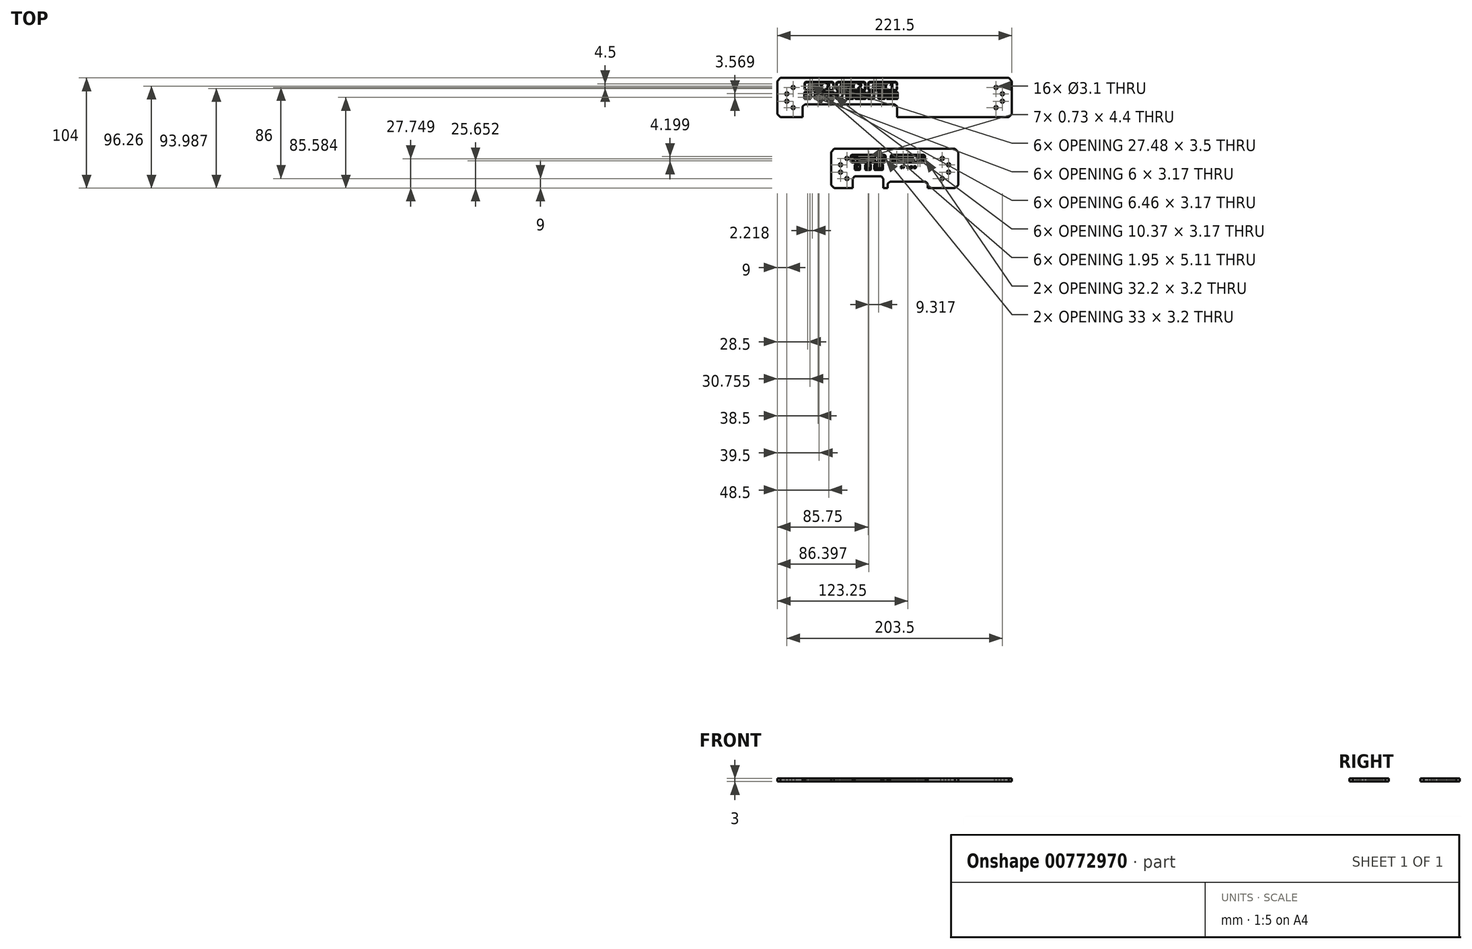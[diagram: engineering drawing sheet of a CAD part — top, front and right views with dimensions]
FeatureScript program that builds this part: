
annotation { "Feature Type Name" : "Feature", "Feature Type Description" : "" }
export const myFeature = defineFeature(function(context is Context, id is Id, definition is map)
    precondition{}
    {
        {
            var Q0;
            Q0=qCreatedBy(makeId("Top.planeOp"),FACE);
            var sketch = newSketch(context, id + "F0", { "sketchPlane" : qUnion([Q0])});
            skLineSegment(sketch, "E0.bottom", {"start": v(110.75, 18.5) * mm, "end": v(-110.75, 18.5) * mm});
            skLineSegment(sketch, "E0.top", {"start": v(110.75, -18.5) * mm, "end": v(-110.75, -18.5) * mm});
            skLineSegment(sketch, "E0.left", {"start": v(110.75, 18.5) * mm, "end": v(110.75, -18.5) * mm});
            skLineSegment(sketch, "E0.right", {"start": v(-110.75, 18.5) * mm, "end": v(-110.75, -18.5) * mm});
            skPoint(sketch, "E0.middle", {"position": v(0, 0) * mm});
            skLineSegment(sketch, "E1", {"start": v(0, 18.5) * mm, "end": v(0, -18.5) * mm, "construction": true});
            skCircle(sketch, "E2", {"center": v(95.75, 9.5) * mm, "radius": 1.55 * mm});
            skCircle(sketch, "E3", {"center": v(101.75, 3.5) * mm, "radius": 1.55 * mm});
            skCircle(sketch, "E4.MirrorC", {"center": v(-95.75, 9.5) * mm, "radius": 1.55 * mm});
            skCircle(sketch, "E5.MirrorC", {"center": v(-101.75, 3.5) * mm, "radius": 1.55 * mm});
            skLineSegment(sketch, "E6.bottom", {"start": v(-85.75, -18.5) * mm, "end": v(1.25, -18.5) * mm});
            skLineSegment(sketch, "E6.top", {"start": v(-85.75, -6.5) * mm, "end": v(1.25, -6.5) * mm});
            skLineSegment(sketch, "E6.left", {"start": v(-85.75, -18.5) * mm, "end": v(-85.75, -6.5) * mm});
            skLineSegment(sketch, "E6.right", {"start": v(1.25, -18.5) * mm, "end": v(1.25, -6.5) * mm});
            skLineSegment(sketch, "E7", {"start": v(-82.25, -6.5) * mm, "end": v(-82.25, -18.5) * mm, "construction": true});
            skLineSegment(sketch, "E8.1.0.0", {"start": v(-72.25, -6.5) * mm, "end": v(-72.25, -18.5) * mm, "construction": true});
            skLineSegment(sketch, "E8.2.0.0", {"start": v(-62.25, -6.5) * mm, "end": v(-62.25, -18.5) * mm, "construction": true});
            skLineSegment(sketch, "E8.3.0.0", {"start": v(-52.25, -6.5) * mm, "end": v(-52.25, -18.5) * mm, "construction": true});
            skLineSegment(sketch, "E8.4.0.0", {"start": v(-42.25, -6.5) * mm, "end": v(-42.25, -18.5) * mm, "construction": true});
            skLineSegment(sketch, "E8.5.0.0", {"start": v(-32.25, -6.5) * mm, "end": v(-32.25, -18.5) * mm, "construction": true});
            skLineSegment(sketch, "E8.6.0.0", {"start": v(-22.25, -6.5) * mm, "end": v(-22.25, -18.5) * mm, "construction": true});
            skLineSegment(sketch, "E8.7.0.0", {"start": v(-12.25, -6.5) * mm, "end": v(-12.25, -18.5) * mm, "construction": true});
            skLineSegment(sketch, "E8.direction1", {"start": v(-82.25, -18.5) * mm, "end": v(-72.25, -18.5) * mm, "construction": true});
            skText(sketch, "E9", { "text": "L", "fontName": "AllertaStencil-Regular.ttf"});
            skText(sketch, "E10", { "text": "N", "fontName": "AllertaStencil-Regular.ttf"});
            skText(sketch, "E11", { "text": "PG", "fontName": "AllertaStencil-Regular.ttf"});
            skText(sketch, "E12", { "text": "L", "fontName": "AllertaStencil-Regular.ttf"});
            skText(sketch, "E13", { "text": "N", "fontName": "AllertaStencil-Regular.ttf"});
            skText(sketch, "E14", { "text": "PG", "fontName": "AllertaStencil-Regular.ttf"});
            skText(sketch, "E15", { "text": "L", "fontName": "AllertaStencil-Regular.ttf"});
            skText(sketch, "E16", { "text": "N", "fontName": "AllertaStencil-Regular.ttf"});
            skText(sketch, "E17", { "text": "PG", "fontName": "AllertaStencil-Regular.ttf"});
            skLineSegment(sketch, "E18.0.8.0", {"start": v(-2.25, -6.5) * mm, "end": v(-2.25, -18.5) * mm, "construction": true});
            skText(sketch, "E19", { "text": "OUT 1", "fontName": "AllertaStencil-Regular.ttf"});
            skText(sketch, "E20", { "text": "OUT 2", "fontName": "AllertaStencil-Regular.ttf"});
            skText(sketch, "E21", { "text": "OUT 3", "fontName": "AllertaStencil-Regular.ttf"});
            skLineSegment(sketch, "E22", {"start": v(-110.75, 0) * mm, "end": v(110.75, 0) * mm, "construction": true});
            skCircle(sketch, "E23.MirrorC", {"center": v(95.75, -9.5) * mm, "radius": 1.55 * mm});
            skCircle(sketch, "E24.MirrorC", {"center": v(101.75, -3.5) * mm, "radius": 1.55 * mm});
            skCircle(sketch, "E25.MirrorC", {"center": v(-95.75, -9.5) * mm, "radius": 1.55 * mm});
            skCircle(sketch, "E26.MirrorC", {"center": v(-101.75, -3.5) * mm, "radius": 1.55 * mm});
            skLineSegment(sketch, "E27", {"start": v(1.25, -6.5) * mm, "end": v(2.25, -6.5) * mm});
            skLineSegment(sketch, "E28", {"start": v(2.25, -6.5) * mm, "end": v(2.25, -18.5) * mm});
            skLineSegment(sketch, "E29", {"start": v(-85.75, -6.5) * mm, "end": v(-86.75, -6.5) * mm});
            skLineSegment(sketch, "E30", {"start": v(-86.75, -6.5) * mm, "end": v(-86.75, -18.5) * mm});
            skLineSegment(sketch, "E31.bottom", {"start": v(60, -48.5) * mm, "end": v(-60, -48.5) * mm});
            skLineSegment(sketch, "E31.top", {"start": v(60, -85.5) * mm, "end": v(-60, -85.5) * mm});
            skLineSegment(sketch, "E31.left", {"start": v(60, -48.5) * mm, "end": v(60, -85.5) * mm});
            skLineSegment(sketch, "E31.right", {"start": v(-60, -48.5) * mm, "end": v(-60, -85.5) * mm});
            skPoint(sketch, "E31.middle", {"position": v(0, -67) * mm});
            skLineSegment(sketch, "E32", {"start": v(-60, -67) * mm, "end": v(60, -67) * mm, "construction": true});
            skLineSegment(sketch, "E33", {"start": v(0, -48.5) * mm, "end": v(0, -85.5) * mm, "construction": true});
            skCircle(sketch, "E34", {"center": v(45, -57.5) * mm, "radius": 1.55 * mm});
            skCircle(sketch, "E35", {"center": v(51, -63.5) * mm, "radius": 1.55 * mm});
            skCircle(sketch, "E36.MirrorC", {"center": v(45, -76.5) * mm, "radius": 1.55 * mm});
            skCircle(sketch, "E37.MirrorC", {"center": v(51, -70.5) * mm, "radius": 1.55 * mm});
            skCircle(sketch, "E38.MirrorC", {"center": v(-45, -57.5) * mm, "radius": 1.55 * mm});
            skCircle(sketch, "E39.MirrorC", {"center": v(-51, -63.5) * mm, "radius": 1.55 * mm});
            skCircle(sketch, "E40.MirrorC", {"center": v(-51, -70.5) * mm, "radius": 1.55 * mm});
            skCircle(sketch, "E41.MirrorC", {"center": v(-45, -76.5) * mm, "radius": 1.55 * mm});
            skLineSegment(sketch, "E42", {"start": v(-39.5, -85.5) * mm, "end": v(-39.5, -74.5) * mm});
            skLineSegment(sketch, "E43", {"start": v(-39.5, -74.5) * mm, "end": v(-10.5, -74.5) * mm});
            skLineSegment(sketch, "E44", {"start": v(-10.5, -74.5) * mm, "end": v(-10.5, -85.5) * mm});
            skLineSegment(sketch, "E45", {"start": v(-6.4, -85.5) * mm, "end": v(-6.4, -79.5) * mm});
            skLineSegment(sketch, "E46", {"start": v(-6.4, -79.5) * mm, "end": v(31.4, -79.5) * mm});
            skLineSegment(sketch, "E47", {"start": v(31.4, -79.5) * mm, "end": v(31.4, -85.5) * mm});
            skLineSegment(sketch, "E48", {"start": v(-38.5, -74.5) * mm, "end": v(-38.5, -85.5) * mm});
            skLineSegment(sketch, "E49", {"start": v(-11.5, -74.5) * mm, "end": v(-11.5, -85.5) * mm});
            skLineSegment(sketch, "E50", {"start": v(-35, -74.5) * mm, "end": v(-35, -85.5) * mm});
            skLineSegment(sketch, "E51", {"start": v(-25, -74.5) * mm, "end": v(-25, -85.5) * mm});
            skLineSegment(sketch, "E52", {"start": v(-15, -74.5) * mm, "end": v(-15, -85.5) * mm});
            skText(sketch, "E53", { "text": "L", "fontName": "AllertaStencil-Regular.ttf"});
            skText(sketch, "E54", { "text": "N", "fontName": "AllertaStencil-Regular.ttf"});
            skText(sketch, "E55", { "text": "POWER IN", "fontName": "AllertaStencil-Regular.ttf"});
            skLineSegment(sketch, "E56.bottom", {"start": v(-84.49, 14.24) * mm, "end": v(-58.01, 14.24) * mm});
            skLineSegment(sketch, "E56.top", {"start": v(-84.49, 7.24) * mm, "end": v(-58.01, 7.24) * mm});
            skLineSegment(sketch, "E56.left", {"start": v(-84.49, 14.24) * mm, "end": v(-84.49, 7.24) * mm});
            skLineSegment(sketch, "E56.right", {"start": v(-58.01, 14.24) * mm, "end": v(-58.01, 7.24) * mm});
            skLineSegment(sketch, "E57.bottom", {"start": v(-57.51, 14.74) * mm, "end": v(-84.99, 14.74) * mm});
            skLineSegment(sketch, "E57.top", {"start": v(-57.51, 6.74) * mm, "end": v(-84.99, 6.74) * mm});
            skLineSegment(sketch, "E57.left", {"start": v(-57.51, 14.74) * mm, "end": v(-57.51, 6.74) * mm});
            skLineSegment(sketch, "E57.right", {"start": v(-84.99, 14.74) * mm, "end": v(-84.99, 6.74) * mm});
            skPoint(sketch, "E57.middle", {"position": v(-71.25, 10.74) * mm});
            skLineSegment(sketch, "E58", {"start": v(-84.99, 10.74) * mm, "end": v(-57.51, 10.74) * mm, "construction": true});
            skLineSegment(sketch, "E59", {"start": v(-84.49, 11.24) * mm, "end": v(-84.99, 11.24) * mm});
            skLineSegment(sketch, "E60.MirrorCS", {"start": v(-84.49, 10.24) * mm, "end": v(-84.99, 10.24) * mm});
            skLineSegment(sketch, "E61.MirrorCS", {"start": v(-58.01, 11.24) * mm, "end": v(-57.51, 11.24) * mm});
            skLineSegment(sketch, "E62.MirrorCS", {"start": v(-58.01, 10.24) * mm, "end": v(-57.51, 10.24) * mm});
            skLineSegment(sketch, "E63.1.0.0", {"start": v(-27.51, 14.74) * mm, "end": v(-54.99, 14.74) * mm});
            skLineSegment(sketch, "E63.1.0.1", {"start": v(-54.49, 14.24) * mm, "end": v(-28.01, 14.24) * mm});
            skLineSegment(sketch, "E63.1.0.2", {"start": v(-54.49, 7.24) * mm, "end": v(-28.01, 7.24) * mm});
            skLineSegment(sketch, "E63.1.0.3", {"start": v(-27.51, 6.74) * mm, "end": v(-54.99, 6.74) * mm});
            skLineSegment(sketch, "E63.1.0.4", {"start": v(-28.01, 14.24) * mm, "end": v(-28.01, 7.24) * mm});
            skLineSegment(sketch, "E63.1.0.5", {"start": v(-27.51, 14.74) * mm, "end": v(-27.51, 6.74) * mm});
            skLineSegment(sketch, "E63.1.0.6", {"start": v(-28.01, 10.24) * mm, "end": v(-27.51, 10.24) * mm});
            skLineSegment(sketch, "E63.1.0.7", {"start": v(-28.01, 11.24) * mm, "end": v(-27.51, 11.24) * mm});
            skLineSegment(sketch, "E63.1.0.8", {"start": v(-54.49, 10.24) * mm, "end": v(-54.99, 10.24) * mm});
            skLineSegment(sketch, "E63.1.0.9", {"start": v(-54.99, 14.74) * mm, "end": v(-54.99, 6.74) * mm});
            skLineSegment(sketch, "E63.1.0.10", {"start": v(-54.49, 14.24) * mm, "end": v(-54.49, 7.24) * mm});
            skLineSegment(sketch, "E63.1.0.11", {"start": v(-54.49, 11.24) * mm, "end": v(-54.99, 11.24) * mm});
            skLineSegment(sketch, "E63.2.0.0", {"start": v(2.49, 14.74) * mm, "end": v(-24.99, 14.74) * mm});
            skLineSegment(sketch, "E63.2.0.1", {"start": v(-24.49, 14.24) * mm, "end": v(1.99, 14.24) * mm});
            skLineSegment(sketch, "E63.2.0.2", {"start": v(-24.49, 7.24) * mm, "end": v(1.99, 7.24) * mm});
            skLineSegment(sketch, "E63.2.0.3", {"start": v(2.49, 6.74) * mm, "end": v(-24.99, 6.74) * mm});
            skLineSegment(sketch, "E63.2.0.4", {"start": v(1.99, 14.24) * mm, "end": v(1.99, 7.24) * mm});
            skLineSegment(sketch, "E63.2.0.5", {"start": v(2.49, 14.74) * mm, "end": v(2.49, 6.74) * mm});
            skLineSegment(sketch, "E63.2.0.6", {"start": v(1.99, 10.24) * mm, "end": v(2.49, 10.24) * mm});
            skLineSegment(sketch, "E63.2.0.7", {"start": v(1.99, 11.24) * mm, "end": v(2.49, 11.24) * mm});
            skLineSegment(sketch, "E63.2.0.8", {"start": v(-24.49, 10.24) * mm, "end": v(-24.99, 10.24) * mm});
            skLineSegment(sketch, "E63.2.0.9", {"start": v(-24.99, 14.74) * mm, "end": v(-24.99, 6.74) * mm});
            skLineSegment(sketch, "E63.2.0.10", {"start": v(-24.49, 14.24) * mm, "end": v(-24.49, 7.24) * mm});
            skLineSegment(sketch, "E63.2.0.11", {"start": v(-24.49, 11.24) * mm, "end": v(-24.99, 11.24) * mm});
            skLineSegment(sketch, "E63.direction1", {"start": v(-84.99, 14.74) * mm, "end": v(-54.99, 14.74) * mm, "construction": true});
            skLineSegment(sketch, "E64.bottom", {"start": v(-79.75, 4.74) * mm, "end": v(-84.75, 4.74) * mm});
            skLineSegment(sketch, "E64.top", {"start": v(-79.75, -1) * mm, "end": v(-84.75, -1) * mm});
            skLineSegment(sketch, "E64.left", {"start": v(-79.75, 4.74) * mm, "end": v(-79.75, -1) * mm});
            skLineSegment(sketch, "E64.right", {"start": v(-84.75, 4.74) * mm, "end": v(-84.75, -1) * mm});
            skPoint(sketch, "E64.middle", {"position": v(-82.25, 1.87) * mm});
            skLineSegment(sketch, "E65.bottom", {"start": v(-69.52, 4.74) * mm, "end": v(-74.98, 4.74) * mm});
            skLineSegment(sketch, "E65.top", {"start": v(-69.52, -1) * mm, "end": v(-74.98, -1) * mm});
            skLineSegment(sketch, "E65.left", {"start": v(-69.52, 4.74) * mm, "end": v(-69.52, -1) * mm});
            skLineSegment(sketch, "E65.right", {"start": v(-74.98, 4.74) * mm, "end": v(-74.98, -1) * mm});
            skPoint(sketch, "E65.middle", {"position": v(-72.25, 1.87) * mm});
            skLineSegment(sketch, "E66.bottom", {"start": v(-66.93, 4.74) * mm, "end": v(-57.57, 4.74) * mm});
            skLineSegment(sketch, "E66.top", {"start": v(-66.93, -1) * mm, "end": v(-57.57, -1) * mm});
            skLineSegment(sketch, "E66.left", {"start": v(-66.93, 4.74) * mm, "end": v(-66.93, -1) * mm});
            skLineSegment(sketch, "E66.right", {"start": v(-57.57, 4.74) * mm, "end": v(-57.57, -1) * mm});
            skLineSegment(sketch, "E67.bottom", {"start": v(-79.25, 5.24) * mm, "end": v(-85.25, 5.24) * mm});
            skLineSegment(sketch, "E67.top", {"start": v(-79.25, -1.5) * mm, "end": v(-85.25, -1.5) * mm});
            skLineSegment(sketch, "E67.left", {"start": v(-79.25, 5.24) * mm, "end": v(-79.25, -1.5) * mm});
            skLineSegment(sketch, "E67.right", {"start": v(-85.25, 5.24) * mm, "end": v(-85.25, -1.5) * mm});
            skLineSegment(sketch, "E68.bottom", {"start": v(-69.02, 5.24) * mm, "end": v(-75.48, 5.24) * mm});
            skLineSegment(sketch, "E68.top", {"start": v(-69.02, -1.5) * mm, "end": v(-75.48, -1.5) * mm});
            skLineSegment(sketch, "E68.left", {"start": v(-69.02, 5.24) * mm, "end": v(-69.02, -1.5) * mm});
            skLineSegment(sketch, "E68.right", {"start": v(-75.48, 5.24) * mm, "end": v(-75.48, -1.5) * mm});
            skPoint(sketch, "E69.firstSnap0", {"position": v(-72.25, 5.24) * mm});
            skLineSegment(sketch, "E69.bottom", {"start": v(-67.43, 5.24) * mm, "end": v(-57.07, 5.24) * mm});
            skLineSegment(sketch, "E69.top", {"start": v(-67.43, -1.5) * mm, "end": v(-57.07, -1.5) * mm});
            skLineSegment(sketch, "E69.left", {"start": v(-67.43, 5.24) * mm, "end": v(-67.43, -1.5) * mm});
            skLineSegment(sketch, "E69.right", {"start": v(-57.07, 5.24) * mm, "end": v(-57.07, -1.5) * mm});
            skLineSegment(sketch, "E70", {"start": v(-85.25, 1.87) * mm, "end": v(-79.25, 1.87) * mm, "construction": true});
            skLineSegment(sketch, "E71", {"start": v(-85.25, 2.07) * mm, "end": v(-84.75, 2.07) * mm});
            skLineSegment(sketch, "E72", {"start": v(-75.48, 2.07) * mm, "end": v(-74.98, 2.07) * mm});
            skLineSegment(sketch, "E73", {"start": v(-67.43, 2.07) * mm, "end": v(-66.93, 2.07) * mm});
            skLineSegment(sketch, "E74.MirrorCS", {"start": v(-85.25, 1.67) * mm, "end": v(-84.75, 1.67) * mm});
            skLineSegment(sketch, "E75.MirrorCS", {"start": v(-75.48, 1.67) * mm, "end": v(-74.98, 1.67) * mm});
            skLineSegment(sketch, "E76.MirrorCS", {"start": v(-67.43, 1.67) * mm, "end": v(-66.93, 1.67) * mm});
            skLineSegment(sketch, "E77.MirrorCS", {"start": v(-79.25, 2.07) * mm, "end": v(-79.75, 2.07) * mm});
            skLineSegment(sketch, "E78.MirrorCS", {"start": v(-79.25, 1.67) * mm, "end": v(-79.75, 1.67) * mm});
            skLineSegment(sketch, "E79.MirrorCS", {"start": v(-69.02, 2.07) * mm, "end": v(-69.52, 2.07) * mm});
            skLineSegment(sketch, "E80.MirrorCS", {"start": v(-69.02, 1.67) * mm, "end": v(-69.52, 1.67) * mm});
            skLineSegment(sketch, "E81.MirrorCS", {"start": v(-57.07, 2.07) * mm, "end": v(-57.57, 2.07) * mm});
            skLineSegment(sketch, "E82.MirrorCS", {"start": v(-57.07, 1.67) * mm, "end": v(-57.57, 1.67) * mm});
            skLineSegment(sketch, "E83.1.0.0", {"start": v(-55.25, 5.24) * mm, "end": v(-55.25, -1.5) * mm});
            skLineSegment(sketch, "E83.1.0.1", {"start": v(-37.43, 5.24) * mm, "end": v(-37.43, -1.5) * mm});
            skLineSegment(sketch, "E83.1.0.2", {"start": v(-39.02, 5.24) * mm, "end": v(-45.48, 5.24) * mm});
            skLineSegment(sketch, "E83.1.0.3", {"start": v(-37.43, 5.24) * mm, "end": v(-27.07, 5.24) * mm});
            skLineSegment(sketch, "E83.1.0.4", {"start": v(-36.93, 4.74) * mm, "end": v(-27.57, 4.74) * mm});
            skLineSegment(sketch, "E83.1.0.5", {"start": v(-39.02, 5.24) * mm, "end": v(-39.02, -1.5) * mm});
            skLineSegment(sketch, "E83.1.0.6", {"start": v(-39.52, -1) * mm, "end": v(-44.98, -1) * mm});
            skLineSegment(sketch, "E83.1.0.7", {"start": v(-36.93, -1) * mm, "end": v(-27.57, -1) * mm});
            skLineSegment(sketch, "E83.1.0.8", {"start": v(-39.02, -1.5) * mm, "end": v(-45.48, -1.5) * mm});
            skLineSegment(sketch, "E83.1.0.9", {"start": v(-49.25, 5.24) * mm, "end": v(-49.25, -1.5) * mm});
            skPoint(sketch, "E83.1.0.10", {"position": v(-42.25, 1.87) * mm});
            skLineSegment(sketch, "E83.1.0.11", {"start": v(-49.25, -1.5) * mm, "end": v(-55.25, -1.5) * mm});
            skLineSegment(sketch, "E83.1.0.12", {"start": v(-54.75, 4.74) * mm, "end": v(-54.75, -1) * mm});
            skLineSegment(sketch, "E83.1.0.13", {"start": v(-36.93, 4.74) * mm, "end": v(-36.93, -1) * mm});
            skLineSegment(sketch, "E83.1.0.14", {"start": v(-49.75, -1) * mm, "end": v(-54.75, -1) * mm});
            skPoint(sketch, "E83.1.0.15", {"position": v(-42.25, 5.24) * mm});
            skLineSegment(sketch, "E83.1.0.16", {"start": v(-44.98, 4.74) * mm, "end": v(-44.98, -1) * mm});
            skPoint(sketch, "E83.1.0.17", {"position": v(-52.25, 1.87) * mm});
            skLineSegment(sketch, "E83.1.0.18", {"start": v(-39.52, 4.74) * mm, "end": v(-39.52, -1) * mm});
            skLineSegment(sketch, "E83.1.0.19", {"start": v(-39.52, 4.74) * mm, "end": v(-44.98, 4.74) * mm});
            skLineSegment(sketch, "E83.1.0.20", {"start": v(-45.48, 5.24) * mm, "end": v(-45.48, -1.5) * mm});
            skLineSegment(sketch, "E83.1.0.21", {"start": v(-27.07, 5.24) * mm, "end": v(-27.07, -1.5) * mm});
            skLineSegment(sketch, "E83.1.0.22", {"start": v(-37.43, -1.5) * mm, "end": v(-27.07, -1.5) * mm});
            skLineSegment(sketch, "E83.1.0.23", {"start": v(-49.75, 4.74) * mm, "end": v(-54.75, 4.74) * mm});
            skLineSegment(sketch, "E83.1.0.24", {"start": v(-49.75, 4.74) * mm, "end": v(-49.75, -1) * mm});
            skLineSegment(sketch, "E83.1.0.25", {"start": v(-49.25, 5.24) * mm, "end": v(-55.25, 5.24) * mm});
            skLineSegment(sketch, "E83.1.0.26", {"start": v(-27.57, 4.74) * mm, "end": v(-27.57, -1) * mm});
            skPoint(sketch, "E83.1.0.27", {"position": v(-52.25, 1.87) * mm});
            skLineSegment(sketch, "E83.1.0.28", {"start": v(-45.48, 2.07) * mm, "end": v(-44.98, 2.07) * mm});
            skLineSegment(sketch, "E83.1.0.29", {"start": v(-45.48, 1.67) * mm, "end": v(-44.98, 1.67) * mm});
            skLineSegment(sketch, "E83.1.0.30", {"start": v(-39.02, 1.67) * mm, "end": v(-39.52, 1.67) * mm});
            skLineSegment(sketch, "E83.1.0.31", {"start": v(-27.07, 1.67) * mm, "end": v(-27.57, 1.67) * mm});
            skLineSegment(sketch, "E83.1.0.32", {"start": v(-55.25, 1.67) * mm, "end": v(-54.75, 1.67) * mm});
            skLineSegment(sketch, "E83.1.0.33", {"start": v(-55.25, 2.07) * mm, "end": v(-54.75, 2.07) * mm});
            skLineSegment(sketch, "E83.1.0.34", {"start": v(-37.43, 1.67) * mm, "end": v(-36.93, 1.67) * mm});
            skLineSegment(sketch, "E83.1.0.35", {"start": v(-27.07, 2.07) * mm, "end": v(-27.57, 2.07) * mm});
            skLineSegment(sketch, "E83.1.0.36", {"start": v(-37.43, 2.07) * mm, "end": v(-36.93, 2.07) * mm});
            skLineSegment(sketch, "E83.1.0.37", {"start": v(-39.02, 2.07) * mm, "end": v(-39.52, 2.07) * mm});
            skLineSegment(sketch, "E83.1.0.38", {"start": v(-49.25, 1.67) * mm, "end": v(-49.75, 1.67) * mm});
            skLineSegment(sketch, "E83.1.0.39", {"start": v(-49.25, 2.07) * mm, "end": v(-49.75, 2.07) * mm});
            skLineSegment(sketch, "E83.2.0.0", {"start": v(-25.25, 5.24) * mm, "end": v(-25.25, -1.5) * mm});
            skLineSegment(sketch, "E83.2.0.1", {"start": v(-7.43, 5.24) * mm, "end": v(-7.43, -1.5) * mm});
            skLineSegment(sketch, "E83.2.0.2", {"start": v(-9.02, 5.24) * mm, "end": v(-15.48, 5.24) * mm});
            skLineSegment(sketch, "E83.2.0.3", {"start": v(-7.43, 5.24) * mm, "end": v(2.93, 5.24) * mm});
            skLineSegment(sketch, "E83.2.0.4", {"start": v(-6.93, 4.74) * mm, "end": v(2.43, 4.74) * mm});
            skLineSegment(sketch, "E83.2.0.5", {"start": v(-9.02, 5.24) * mm, "end": v(-9.02, -1.5) * mm});
            skLineSegment(sketch, "E83.2.0.6", {"start": v(-9.52, -1) * mm, "end": v(-14.98, -1) * mm});
            skLineSegment(sketch, "E83.2.0.7", {"start": v(-6.93, -1) * mm, "end": v(2.43, -1) * mm});
            skLineSegment(sketch, "E83.2.0.8", {"start": v(-9.02, -1.5) * mm, "end": v(-15.48, -1.5) * mm});
            skLineSegment(sketch, "E83.2.0.9", {"start": v(-19.25, 5.24) * mm, "end": v(-19.25, -1.5) * mm});
            skPoint(sketch, "E83.2.0.10", {"position": v(-12.25, 1.87) * mm});
            skLineSegment(sketch, "E83.2.0.11", {"start": v(-19.25, -1.5) * mm, "end": v(-25.25, -1.5) * mm});
            skLineSegment(sketch, "E83.2.0.12", {"start": v(-24.75, 4.74) * mm, "end": v(-24.75, -1) * mm});
            skLineSegment(sketch, "E83.2.0.13", {"start": v(-6.93, 4.74) * mm, "end": v(-6.93, -1) * mm});
            skLineSegment(sketch, "E83.2.0.14", {"start": v(-19.75, -1) * mm, "end": v(-24.75, -1) * mm});
            skPoint(sketch, "E83.2.0.15", {"position": v(-12.25, 5.24) * mm});
            skLineSegment(sketch, "E83.2.0.16", {"start": v(-14.98, 4.74) * mm, "end": v(-14.98, -1) * mm});
            skPoint(sketch, "E83.2.0.17", {"position": v(-22.25, 1.87) * mm});
            skLineSegment(sketch, "E83.2.0.18", {"start": v(-9.52, 4.74) * mm, "end": v(-9.52, -1) * mm});
            skLineSegment(sketch, "E83.2.0.19", {"start": v(-9.52, 4.74) * mm, "end": v(-14.98, 4.74) * mm});
            skLineSegment(sketch, "E83.2.0.20", {"start": v(-15.48, 5.24) * mm, "end": v(-15.48, -1.5) * mm});
            skLineSegment(sketch, "E83.2.0.21", {"start": v(2.93, 5.24) * mm, "end": v(2.93, -1.5) * mm});
            skLineSegment(sketch, "E83.2.0.22", {"start": v(-7.43, -1.5) * mm, "end": v(2.93, -1.5) * mm});
            skLineSegment(sketch, "E83.2.0.23", {"start": v(-19.75, 4.74) * mm, "end": v(-24.75, 4.74) * mm});
            skLineSegment(sketch, "E83.2.0.24", {"start": v(-19.75, 4.74) * mm, "end": v(-19.75, -1) * mm});
            skLineSegment(sketch, "E83.2.0.25", {"start": v(-19.25, 5.24) * mm, "end": v(-25.25, 5.24) * mm});
            skLineSegment(sketch, "E83.2.0.26", {"start": v(2.43, 4.74) * mm, "end": v(2.43, -1) * mm});
            skPoint(sketch, "E83.2.0.27", {"position": v(-22.25, 1.87) * mm});
            skLineSegment(sketch, "E83.2.0.28", {"start": v(-15.48, 2.07) * mm, "end": v(-14.98, 2.07) * mm});
            skLineSegment(sketch, "E83.2.0.29", {"start": v(-15.48, 1.67) * mm, "end": v(-14.98, 1.67) * mm});
            skLineSegment(sketch, "E83.2.0.30", {"start": v(-9.02, 1.67) * mm, "end": v(-9.52, 1.67) * mm});
            skLineSegment(sketch, "E83.2.0.31", {"start": v(2.93, 1.67) * mm, "end": v(2.43, 1.67) * mm});
            skLineSegment(sketch, "E83.2.0.32", {"start": v(-25.25, 1.67) * mm, "end": v(-24.75, 1.67) * mm});
            skLineSegment(sketch, "E83.2.0.33", {"start": v(-25.25, 2.07) * mm, "end": v(-24.75, 2.07) * mm});
            skLineSegment(sketch, "E83.2.0.34", {"start": v(-7.43, 1.67) * mm, "end": v(-6.93, 1.67) * mm});
            skLineSegment(sketch, "E83.2.0.35", {"start": v(2.93, 2.07) * mm, "end": v(2.43, 2.07) * mm});
            skLineSegment(sketch, "E83.2.0.36", {"start": v(-7.43, 2.07) * mm, "end": v(-6.93, 2.07) * mm});
            skLineSegment(sketch, "E83.2.0.37", {"start": v(-9.02, 2.07) * mm, "end": v(-9.52, 2.07) * mm});
            skLineSegment(sketch, "E83.2.0.38", {"start": v(-19.25, 1.67) * mm, "end": v(-19.75, 1.67) * mm});
            skLineSegment(sketch, "E83.2.0.39", {"start": v(-19.25, 2.07) * mm, "end": v(-19.75, 2.07) * mm});
            skLineSegment(sketch, "E83.direction1", {"start": v(-85.25, -1.5) * mm, "end": v(-55.25, -1.5) * mm, "construction": true});
            skLineSegment(sketch, "E84.bottom", {"start": v(-9, -54.55) * mm, "end": v(-41, -54.55) * mm});
            skLineSegment(sketch, "E84.top", {"start": v(-9, -60.95) * mm, "end": v(-41, -60.95) * mm});
            skLineSegment(sketch, "E84.left", {"start": v(-9, -54.55) * mm, "end": v(-9, -60.95) * mm});
            skLineSegment(sketch, "E84.right", {"start": v(-41, -54.55) * mm, "end": v(-41, -60.95) * mm});
            skPoint(sketch, "E84.middle", {"position": v(-25, -57.75) * mm});
            skLineSegment(sketch, "E85.bottom", {"start": v(-33, -63.45) * mm, "end": v(-37, -63.45) * mm});
            skLineSegment(sketch, "E85.top", {"start": v(-33, -68) * mm, "end": v(-37, -68) * mm});
            skLineSegment(sketch, "E85.left", {"start": v(-33, -63.45) * mm, "end": v(-33, -68) * mm});
            skLineSegment(sketch, "E85.right", {"start": v(-37, -63.45) * mm, "end": v(-37, -68) * mm});
            skPoint(sketch, "E85.middle", {"position": v(-35, -65.72) * mm});
            skLineSegment(sketch, "E86.bottom", {"start": v(-8.5, -54.05) * mm, "end": v(-41.5, -54.05) * mm});
            skLineSegment(sketch, "E86.top", {"start": v(-8.5, -61.45) * mm, "end": v(-41.5, -61.45) * mm});
            skLineSegment(sketch, "E86.left", {"start": v(-8.5, -54.05) * mm, "end": v(-8.5, -61.45) * mm});
            skLineSegment(sketch, "E86.right", {"start": v(-41.5, -54.05) * mm, "end": v(-41.5, -61.45) * mm});
            skLineSegment(sketch, "E87.bottom", {"start": v(-27.17, -63.45) * mm, "end": v(-22.83, -63.45) * mm});
            skLineSegment(sketch, "E87.top", {"start": v(-27.17, -68) * mm, "end": v(-22.83, -68) * mm});
            skLineSegment(sketch, "E87.left", {"start": v(-27.17, -63.45) * mm, "end": v(-27.17, -68) * mm});
            skLineSegment(sketch, "E87.right", {"start": v(-22.83, -63.45) * mm, "end": v(-22.83, -68) * mm});
            skText(sketch, "E88", { "text": "PG", "fontName": "AllertaStencil-Regular.ttf"});
            skLineSegment(sketch, "E89.bottom", {"start": v(-18.64, -63.45) * mm, "end": v(-11.36, -63.45) * mm});
            skLineSegment(sketch, "E89.top", {"start": v(-18.64, -68) * mm, "end": v(-11.36, -68) * mm});
            skLineSegment(sketch, "E89.left", {"start": v(-18.64, -63.45) * mm, "end": v(-18.64, -68) * mm});
            skLineSegment(sketch, "E89.right", {"start": v(-11.36, -63.45) * mm, "end": v(-11.36, -68) * mm});
            skLineSegment(sketch, "E90.bottom", {"start": v(-32.5, -62.95) * mm, "end": v(-37.5, -62.95) * mm});
            skLineSegment(sketch, "E90.top", {"start": v(-32.5, -68.5) * mm, "end": v(-37.5, -68.5) * mm});
            skLineSegment(sketch, "E90.left", {"start": v(-32.5, -62.95) * mm, "end": v(-32.5, -68.5) * mm});
            skLineSegment(sketch, "E90.right", {"start": v(-37.5, -62.95) * mm, "end": v(-37.5, -68.5) * mm});
            skLineSegment(sketch, "E91.bottom", {"start": v(-27.67, -62.95) * mm, "end": v(-22.33, -62.95) * mm});
            skLineSegment(sketch, "E91.top", {"start": v(-27.67, -68.5) * mm, "end": v(-22.33, -68.5) * mm});
            skLineSegment(sketch, "E91.left", {"start": v(-27.67, -62.95) * mm, "end": v(-27.67, -68.5) * mm});
            skLineSegment(sketch, "E91.right", {"start": v(-22.33, -62.95) * mm, "end": v(-22.33, -68.5) * mm});
            skLineSegment(sketch, "E92.bottom", {"start": v(-19.14, -62.95) * mm, "end": v(-10.86, -62.95) * mm});
            skLineSegment(sketch, "E92.top", {"start": v(-19.14, -68.5) * mm, "end": v(-10.86, -68.5) * mm});
            skLineSegment(sketch, "E92.left", {"start": v(-19.14, -62.95) * mm, "end": v(-19.14, -68.5) * mm});
            skLineSegment(sketch, "E92.right", {"start": v(-10.86, -62.95) * mm, "end": v(-10.86, -68.5) * mm});
            skLineSegment(sketch, "E93", {"start": v(-37.5, -65.72) * mm, "end": v(-32.5, -65.72) * mm, "construction": true});
            skLineSegment(sketch, "E94", {"start": v(-37.5, -65.52) * mm, "end": v(-37, -65.52) * mm});
            skLineSegment(sketch, "E95", {"start": v(-27.67, -65.52) * mm, "end": v(-27.17, -65.52) * mm});
            skLineSegment(sketch, "E96", {"start": v(-19.14, -65.52) * mm, "end": v(-18.64, -65.52) * mm});
            skLineSegment(sketch, "E97", {"start": v(-41.5, -57.75) * mm, "end": v(-8.5, -57.75) * mm, "construction": true});
            skLineSegment(sketch, "E98.MirrorCS", {"start": v(-37.5, -65.92) * mm, "end": v(-37, -65.92) * mm});
            skLineSegment(sketch, "E99.MirrorCS", {"start": v(-27.67, -65.92) * mm, "end": v(-27.17, -65.92) * mm});
            skLineSegment(sketch, "E100.MirrorCS", {"start": v(-19.14, -65.92) * mm, "end": v(-18.64, -65.92) * mm});
            skLineSegment(sketch, "E101.MirrorCS", {"start": v(-32.5, -65.52) * mm, "end": v(-33, -65.52) * mm});
            skLineSegment(sketch, "E102.MirrorCS", {"start": v(-32.5, -65.92) * mm, "end": v(-33, -65.92) * mm});
            skLineSegment(sketch, "E103.MirrorCS", {"start": v(-22.33, -65.52) * mm, "end": v(-22.83, -65.52) * mm});
            skLineSegment(sketch, "E104.MirrorCS", {"start": v(-22.33, -65.92) * mm, "end": v(-22.83, -65.92) * mm});
            skLineSegment(sketch, "E105.MirrorCS", {"start": v(-10.86, -65.52) * mm, "end": v(-11.36, -65.52) * mm});
            skLineSegment(sketch, "E106.MirrorCS", {"start": v(-10.86, -65.92) * mm, "end": v(-11.36, -65.92) * mm});
            skLineSegment(sketch, "E107", {"start": v(-41.5, -57.25) * mm, "end": v(-41, -57.25) * mm});
            skLineSegment(sketch, "E108.MirrorCS", {"start": v(-41.5, -58.25) * mm, "end": v(-41, -58.25) * mm});
            skLineSegment(sketch, "E109.MirrorCS", {"start": v(-8.5, -57.25) * mm, "end": v(-9, -57.25) * mm});
            skLineSegment(sketch, "E110.MirrorCS", {"start": v(-8.5, -58.25) * mm, "end": v(-9, -58.25) * mm});
            skText(sketch, "E111", { "text": "SIGNAL IN", "fontName": "AllertaStencil-Regular.ttf"});
            skLineSegment(sketch, "E112", {"start": v(12.5, -79.5) * mm, "end": v(12.5, -85.5) * mm, "construction": true});
            skLineSegment(sketch, "E113.bottom", {"start": v(-3.1, -54.55) * mm, "end": v(28.1, -54.55) * mm});
            skLineSegment(sketch, "E113.top", {"start": v(-3.1, -60.95) * mm, "end": v(28.1, -60.95) * mm});
            skLineSegment(sketch, "E113.left", {"start": v(-3.1, -54.55) * mm, "end": v(-3.1, -60.95) * mm});
            skLineSegment(sketch, "E113.right", {"start": v(28.1, -54.55) * mm, "end": v(28.1, -60.95) * mm});
            skLineSegment(sketch, "E114.bottom", {"start": v(-3.6, -54.05) * mm, "end": v(28.6, -54.05) * mm});
            skLineSegment(sketch, "E114.top", {"start": v(-3.6, -61.45) * mm, "end": v(28.6, -61.45) * mm});
            skLineSegment(sketch, "E114.left", {"start": v(-3.6, -54.05) * mm, "end": v(-3.6, -61.45) * mm});
            skLineSegment(sketch, "E114.right", {"start": v(28.6, -54.05) * mm, "end": v(28.6, -61.45) * mm});
            skLineSegment(sketch, "E115", {"start": v(-3.6, -57.75) * mm, "end": v(28.6, -57.75) * mm, "construction": true});
            skLineSegment(sketch, "E116", {"start": v(-3.6, -57.25) * mm, "end": v(-3.1, -57.25) * mm});
            skLineSegment(sketch, "E117.MirrorCS", {"start": v(-3.6, -58.25) * mm, "end": v(-3.1, -58.25) * mm});
            skLineSegment(sketch, "E118.MirrorCS", {"start": v(28.6, -57.25) * mm, "end": v(28.1, -57.25) * mm});
            skLineSegment(sketch, "E119.MirrorCS", {"start": v(28.6, -58.25) * mm, "end": v(28.1, -58.25) * mm});
            skText(sketch, "E120", { "text": "S", "fontName": "AllertaStencil-Regular.ttf"});
            skLineSegment(sketch, "E121", {"start": v(11.72, -65.72) * mm, "end": v(13.28, -65.72) * mm, "construction": true});
            skText(sketch, "E122", { "text": "GND", "fontName": "AllertaStencil-Regular.ttf"});
            skText(sketch, "E123", { "text": "5V", "fontName": "AllertaStencil-Regular.ttf"});
            const initialGuessF0  = {"E9": [-0.08425, -0.0005, 1, 0, 0.00474], "E10": [-0.07448, -0.0005, 1, 0, 0.00474], "E11": [-0.06643, -0.0005, 1, 0, 0.00474], "E12": [-0.05425, -0.0005, 1, 0, 0.00474], "E13": [-0.04448, -0.0005, 1, 0, 0.00474], "E14": [-0.03643, -0.0005, 1, 0, 0.00474], "E15": [-0.02425, -0.0005, 1, 0, 0.00474], "E16": [-0.01448, -0.0005, 1, 0, 0.00474], "E17": [-0.00643, -0.0005, 1, 0, 0.00474], "E19": [-0.0209, 0.00824, 1, 0, 0.005], "E20": [-0.05161, 0.00824, 1, 0, 0.005], "E21": [-0.08149, 0.00824, 1, 0, 0.005], "E53": [-0.0365, -0.0675, 1, 0, 0.00355], "E54": [-0.02667, -0.0675, 1, 0, 0.00355], "E55": [-0.04, -0.05995, 1, 0, 0.0044], "E88": [-0.01814, -0.0675, 1, 0, 0.00355], "E111": [-0.0021, -0.05995, 1, 0, 0.0044], "E120": [0.01172, -0.06672, 1, 0, 0.002], "E122": [0.01454, -0.06672, 1, 0, 0.002], "E123": [0.00566, -0.06672, 1, 0, 0.002]};
            skSetInitialGuess(sketch, initialGuessF0);
            skSolve(sketch);
        }
        {
            var Q0;
            Q0=makeQuery(id+"F0.imprint","IMPRINT",FACE,{"disambiguationData":[TD([[makeQuery(id+"F0.imprint","IMPRINT",EDGE,{"derivedFrom":sQuery(id+"F0.wireOp",EDGE,"E0.bottom")}),1.0]])]});
            var Q1;
            {var subQ0=sQuery(id+"F0.wireOp",EDGE,"E59");Q1=makeQuery(id+"F0.imprint","IMPRINT",FACE,{"disambiguationData":[TD([[makeQuery(id+"F0.imprint","IMPRINT",EDGE,{"derivedFrom":subQ0}),1.0]])]});}
            var Q2;
            {var subQ0=sQuery(id+"F0.wireOp",EDGE,"E61.MirrorCS");Q2=makeQuery(id+"F0.imprint","IMPRINT",FACE,{"disambiguationData":[TD([[makeQuery(id+"F0.imprint","IMPRINT",EDGE,{"derivedFrom":subQ0}),-1.0]])]});}
            var Q3;
            {var subQ0=sQuery(id+"F0.wireOp",EDGE,"E81.MirrorCS");Q3=makeQuery(id+"F0.imprint","IMPRINT",FACE,{"disambiguationData":[TD([[makeQuery(id+"F0.imprint","IMPRINT",EDGE,{"derivedFrom":subQ0}),1.0]])]});}
            var Q4;
            Q4=makeQuery(id+"F0.imprint","IMPRINT",FACE,{"disambiguationData":[TD([[makeQuery(id+"F0.imprint","IMPRINT",EDGE,{"derivedFrom":sQuery(id+"F0.wireOp",EDGE,"E11.sketch_text.stroke-0")}),1.0]])]});
            var Q5;
            {var subQ0=sQuery(id+"F0.wireOp",EDGE,"E73");Q5=makeQuery(id+"F0.imprint","IMPRINT",FACE,{"disambiguationData":[TD([[makeQuery(id+"F0.imprint","IMPRINT",EDGE,{"derivedFrom":subQ0}),-1.0]])]});}
            var Q6;
            {var subQ0=sQuery(id+"F0.wireOp",EDGE,"E79.MirrorCS");Q6=makeQuery(id+"F0.imprint","IMPRINT",FACE,{"disambiguationData":[TD([[makeQuery(id+"F0.imprint","IMPRINT",EDGE,{"derivedFrom":subQ0}),1.0]])]});}
            var Q7;
            {var subQ0=sQuery(id+"F0.wireOp",EDGE,"E72");Q7=makeQuery(id+"F0.imprint","IMPRINT",FACE,{"disambiguationData":[TD([[makeQuery(id+"F0.imprint","IMPRINT",EDGE,{"derivedFrom":subQ0}),-1.0]])]});}
            var Q8;
            {var subQ0=sQuery(id+"F0.wireOp",EDGE,"E77.MirrorCS");Q8=makeQuery(id+"F0.imprint","IMPRINT",FACE,{"disambiguationData":[TD([[makeQuery(id+"F0.imprint","IMPRINT",EDGE,{"derivedFrom":subQ0}),1.0]])]});}
            var Q9;
            {var subQ0=sQuery(id+"F0.wireOp",EDGE,"E71");Q9=makeQuery(id+"F0.imprint","IMPRINT",FACE,{"disambiguationData":[TD([[makeQuery(id+"F0.imprint","IMPRINT",EDGE,{"derivedFrom":subQ0}),-1.0]])]});}
            var Q10;
            Q10=makeQuery(id+"F0.imprint","IMPRINT",FACE,{"disambiguationData":[TD([[makeQuery(id+"F0.imprint","IMPRINT",EDGE,{"derivedFrom":sQuery(id+"F0.wireOp",EDGE,"E9.sketch_text.stroke-0")}),1.0]])]});
            var Q11;
            Q11=makeQuery(id+"F0.imprint","IMPRINT",FACE,{"disambiguationData":[TD([[makeQuery(id+"F0.imprint","IMPRINT",EDGE,{"derivedFrom":sQuery(id+"F0.wireOp",EDGE,"E10.sketch_text.stroke-0")}),1.0]])]});
            var Q12;
            Q12=makeQuery(id+"F0.imprint","IMPRINT",FACE,{"disambiguationData":[TD([[makeQuery(id+"F0.imprint","IMPRINT",EDGE,{"derivedFrom":sQuery(id+"F0.wireOp",EDGE,"E21.sketch_text.stroke-0")}),1.0]])]});
            var Q13;
            Q13=makeQuery(id+"F0.imprint","IMPRINT",FACE,{"disambiguationData":[TD([[makeQuery(id+"F0.imprint","IMPRINT",EDGE,{"derivedFrom":sQuery(id+"F0.wireOp",EDGE,"E20.sketch_text.stroke-0")}),1.0]])]});
            var Q14;
            {var subQ0=sQuery(id+"F0.wireOp",EDGE,"E63.1.0.8");Q14=makeQuery(id+"F0.imprint","IMPRINT",FACE,{"disambiguationData":[TD([[makeQuery(id+"F0.imprint","IMPRINT",EDGE,{"derivedFrom":subQ0}),-1.0]])]});}
            var Q15;
            Q15=makeQuery(id+"F0.imprint","IMPRINT",FACE,{"disambiguationData":[TD([[makeQuery(id+"F0.imprint","IMPRINT",EDGE,{"derivedFrom":sQuery(id+"F0.wireOp",EDGE,"E12.sketch_text.stroke-0")}),1.0]])]});
            var Q16;
            {var subQ0=sQuery(id+"F0.wireOp",EDGE,"E83.1.0.32");Q16=makeQuery(id+"F0.imprint","IMPRINT",FACE,{"disambiguationData":[TD([[makeQuery(id+"F0.imprint","IMPRINT",EDGE,{"derivedFrom":subQ0}),1.0]])]});}
            var Q17;
            {var subQ0=sQuery(id+"F0.wireOp",EDGE,"E83.1.0.38");Q17=makeQuery(id+"F0.imprint","IMPRINT",FACE,{"disambiguationData":[TD([[makeQuery(id+"F0.imprint","IMPRINT",EDGE,{"derivedFrom":subQ0}),-1.0]])]});}
            var Q18;
            Q18=makeQuery(id+"F0.imprint","IMPRINT",FACE,{"disambiguationData":[TD([[makeQuery(id+"F0.imprint","IMPRINT",EDGE,{"derivedFrom":sQuery(id+"F0.wireOp",EDGE,"E19.sketch_text.stroke-0")}),1.0]])]});
            var Q19;
            {var subQ0=sQuery(id+"F0.wireOp",EDGE,"E63.2.0.8");Q19=makeQuery(id+"F0.imprint","IMPRINT",FACE,{"disambiguationData":[TD([[makeQuery(id+"F0.imprint","IMPRINT",EDGE,{"derivedFrom":subQ0}),-1.0]])]});}
            var Q20;
            {var subQ0=sQuery(id+"F0.wireOp",EDGE,"E63.1.0.6");Q20=makeQuery(id+"F0.imprint","IMPRINT",FACE,{"disambiguationData":[TD([[makeQuery(id+"F0.imprint","IMPRINT",EDGE,{"derivedFrom":subQ0}),1.0]])]});}
            var Q21;
            {var subQ0=sQuery(id+"F0.wireOp",EDGE,"E83.1.0.28");Q21=makeQuery(id+"F0.imprint","IMPRINT",FACE,{"disambiguationData":[TD([[makeQuery(id+"F0.imprint","IMPRINT",EDGE,{"derivedFrom":subQ0}),-1.0]])]});}
            var Q22;
            {var subQ0=sQuery(id+"F0.wireOp",EDGE,"E83.1.0.30");Q22=makeQuery(id+"F0.imprint","IMPRINT",FACE,{"disambiguationData":[TD([[makeQuery(id+"F0.imprint","IMPRINT",EDGE,{"derivedFrom":subQ0}),-1.0]])]});}
            var Q23;
            {var subQ0=sQuery(id+"F0.wireOp",EDGE,"E83.1.0.34");Q23=makeQuery(id+"F0.imprint","IMPRINT",FACE,{"disambiguationData":[TD([[makeQuery(id+"F0.imprint","IMPRINT",EDGE,{"derivedFrom":subQ0}),1.0]])]});}
            var Q24;
            {var subQ0=sQuery(id+"F0.wireOp",EDGE,"E83.1.0.31");Q24=makeQuery(id+"F0.imprint","IMPRINT",FACE,{"disambiguationData":[TD([[makeQuery(id+"F0.imprint","IMPRINT",EDGE,{"derivedFrom":subQ0}),-1.0]])]});}
            var Q25;
            {var subQ0=sQuery(id+"F0.wireOp",EDGE,"E83.2.0.32");Q25=makeQuery(id+"F0.imprint","IMPRINT",FACE,{"disambiguationData":[TD([[makeQuery(id+"F0.imprint","IMPRINT",EDGE,{"derivedFrom":subQ0}),1.0]])]});}
            var Q26;
            {var subQ0=sQuery(id+"F0.wireOp",EDGE,"E83.2.0.38");Q26=makeQuery(id+"F0.imprint","IMPRINT",FACE,{"disambiguationData":[TD([[makeQuery(id+"F0.imprint","IMPRINT",EDGE,{"derivedFrom":subQ0}),-1.0]])]});}
            var Q27;
            {var subQ0=sQuery(id+"F0.wireOp",EDGE,"E83.2.0.28");Q27=makeQuery(id+"F0.imprint","IMPRINT",FACE,{"disambiguationData":[TD([[makeQuery(id+"F0.imprint","IMPRINT",EDGE,{"derivedFrom":subQ0}),-1.0]])]});}
            var Q28;
            {var subQ0=sQuery(id+"F0.wireOp",EDGE,"E83.2.0.30");Q28=makeQuery(id+"F0.imprint","IMPRINT",FACE,{"disambiguationData":[TD([[makeQuery(id+"F0.imprint","IMPRINT",EDGE,{"derivedFrom":subQ0}),-1.0]])]});}
            var Q29;
            {var subQ0=sQuery(id+"F0.wireOp",EDGE,"E83.2.0.34");Q29=makeQuery(id+"F0.imprint","IMPRINT",FACE,{"disambiguationData":[TD([[makeQuery(id+"F0.imprint","IMPRINT",EDGE,{"derivedFrom":subQ0}),1.0]])]});}
            var Q30;
            Q30=makeQuery(id+"F0.imprint","IMPRINT",FACE,{"disambiguationData":[TD([[makeQuery(id+"F0.imprint","IMPRINT",EDGE,{"derivedFrom":sQuery(id+"F0.wireOp",EDGE,"E17.sketch_text.stroke-0")}),1.0]])]});
            var Q31;
            Q31=makeQuery(id+"F0.imprint","IMPRINT",FACE,{"disambiguationData":[TD([[makeQuery(id+"F0.imprint","IMPRINT",EDGE,{"derivedFrom":sQuery(id+"F0.wireOp",EDGE,"E16.sketch_text.stroke-0")}),1.0]])]});
            var Q32;
            Q32=makeQuery(id+"F0.imprint","IMPRINT",FACE,{"disambiguationData":[TD([[makeQuery(id+"F0.imprint","IMPRINT",EDGE,{"derivedFrom":sQuery(id+"F0.wireOp",EDGE,"E15.sketch_text.stroke-0")}),1.0]])]});
            var Q33;
            Q33=makeQuery(id+"F0.imprint","IMPRINT",FACE,{"disambiguationData":[TD([[makeQuery(id+"F0.imprint","IMPRINT",EDGE,{"derivedFrom":sQuery(id+"F0.wireOp",EDGE,"E14.sketch_text.stroke-0")}),1.0]])]});
            var Q34;
            Q34=makeQuery(id+"F0.imprint","IMPRINT",FACE,{"disambiguationData":[TD([[makeQuery(id+"F0.imprint","IMPRINT",EDGE,{"derivedFrom":sQuery(id+"F0.wireOp",EDGE,"E13.sketch_text.stroke-0")}),1.0]])]});
            var Q35;
            {var subQ0=sQuery(id+"F0.wireOp",EDGE,"E83.2.0.31");Q35=makeQuery(id+"F0.imprint","IMPRINT",FACE,{"disambiguationData":[TD([[makeQuery(id+"F0.imprint","IMPRINT",EDGE,{"derivedFrom":subQ0}),-1.0]])]});}
            var Q36;
            {var subQ0=sQuery(id+"F0.wireOp",EDGE,"E63.2.0.6");Q36=makeQuery(id+"F0.imprint","IMPRINT",FACE,{"disambiguationData":[TD([[makeQuery(id+"F0.imprint","IMPRINT",EDGE,{"derivedFrom":subQ0}),1.0]])]});}
            extrude(context, id + "F1", {"entities" : qUnion([Q0, Q1, Q2, Q3, Q4, Q5, Q6, Q7, Q8, Q9, Q10, Q11, Q12, Q13, Q14, Q15, Q16, Q17, Q18, Q19, Q20, Q21, Q22, Q23, Q24, Q25, Q26, Q27, Q28, Q29, Q30, Q31, Q32, Q33, Q34, Q35, Q36]), "depth" : 3 * mm, "offsetDistance" : 25 * mm});
        }
        {
            var Q0;
            Q0=makeQuery(id+"F1.opExtrude","SWEPT_EDGE",EDGE,{"disambiguationData":[OSD([sQuery(id+"F0.wireOp",EDGE,"E0.bottom"),sQuery(id+"F0.wireOp",EDGE,"E0.right")])]});
            var Q1;
            Q1=makeQuery(id+"F1.opExtrude","SWEPT_EDGE",EDGE,{"disambiguationData":[OSD([sQuery(id+"F0.wireOp",EDGE,"E0.top"),sQuery(id+"F0.wireOp",EDGE,"E0.right")])]});
            var Q2;
            Q2=makeQuery(id+"F1.opExtrude","SWEPT_EDGE",EDGE,{"disambiguationData":[OSD([sQuery(id+"F0.wireOp",EDGE,"E0.bottom"),sQuery(id+"F0.wireOp",EDGE,"E0.left")])]});
            var Q3;
            Q3=makeQuery(id+"F1.opExtrude","SWEPT_EDGE",EDGE,{"disambiguationData":[OSD([sQuery(id+"F0.wireOp",EDGE,"E0.top"),sQuery(id+"F0.wireOp",EDGE,"E0.left")])]});
            chamfer(context, id + "F2", {"entities" : qUnion([Q0, Q1, Q2, Q3]), "width" : 3 * mm, "tangentPropagation" : true});
        }
        {
            var Q0;
            Q0=makeQuery(id+"F1.opExtrude","SWEPT_EDGE",EDGE,{"disambiguationData":[OSD([sQuery(id+"F0.wireOp",EDGE,"E29"),sQuery(id+"F0.wireOp",EDGE,"E30")])]});
            var Q1;
            Q1=makeQuery(id+"F1.opExtrude","SWEPT_EDGE",EDGE,{"disambiguationData":[OSD([sQuery(id+"F0.wireOp",EDGE,"E27"),sQuery(id+"F0.wireOp",EDGE,"E28")])]});
            chamfer(context, id + "F3", {"entities" : qUnion([Q0, Q1]), "width" : 2 * mm, "tangentPropagation" : true});
        }
        {
            var Q0;
            Q0=makeQuery(id+"F1.opExtrude","SWEPT_EDGE",EDGE,{"disambiguationData":[OSD([sQuery(id+"F0.wireOp",EDGE,"E57.bottom"),sQuery(id+"F0.wireOp",EDGE,"E57.right")])]});
            var Q1;
            Q1=makeQuery(id+"F1.opExtrude","SWEPT_EDGE",EDGE,{"disambiguationData":[OSD([sQuery(id+"F0.wireOp",EDGE,"E56.top"),sQuery(id+"F0.wireOp",EDGE,"E56.left")])]});
            var Q2;
            Q2=makeQuery(id+"F1.opExtrude","SWEPT_EDGE",EDGE,{"disambiguationData":[OSD([sQuery(id+"F0.wireOp",EDGE,"E56.top"),sQuery(id+"F0.wireOp",EDGE,"E56.right")])]});
            var Q3;
            Q3=makeQuery(id+"F1.opExtrude","SWEPT_EDGE",EDGE,{"disambiguationData":[OSD([sQuery(id+"F0.wireOp",EDGE,"E56.bottom"),sQuery(id+"F0.wireOp",EDGE,"E56.right")])]});
            var Q4;
            Q4=makeQuery(id+"F1.opExtrude","SWEPT_EDGE",EDGE,{"disambiguationData":[OSD([sQuery(id+"F0.wireOp",EDGE,"E57.bottom"),sQuery(id+"F0.wireOp",EDGE,"E57.left")])]});
            var Q5;
            Q5=makeQuery(id+"F1.opExtrude","SWEPT_EDGE",EDGE,{"disambiguationData":[OSD([sQuery(id+"F0.wireOp",EDGE,"E56.bottom"),sQuery(id+"F0.wireOp",EDGE,"E56.left")])]});
            var Q6;
            Q6=makeQuery(id+"F1.opExtrude","SWEPT_EDGE",EDGE,{"disambiguationData":[OSD([sQuery(id+"F0.wireOp",EDGE,"E57.top"),sQuery(id+"F0.wireOp",EDGE,"E57.left")])]});
            var Q7;
            Q7=makeQuery(id+"F1.opExtrude","SWEPT_EDGE",EDGE,{"disambiguationData":[OSD([sQuery(id+"F0.wireOp",EDGE,"E57.top"),sQuery(id+"F0.wireOp",EDGE,"E57.right")])]});
            var Q8;
            Q8=makeQuery(id+"F1.opExtrude","SWEPT_EDGE",EDGE,{"disambiguationData":[OSD([sQuery(id+"F0.wireOp",EDGE,"E63.1.0.3"),sQuery(id+"F0.wireOp",EDGE,"E63.1.0.9")])]});
            var Q9;
            Q9=makeQuery(id+"F1.opExtrude","SWEPT_EDGE",EDGE,{"disambiguationData":[OSD([sQuery(id+"F0.wireOp",EDGE,"E63.1.0.1"),sQuery(id+"F0.wireOp",EDGE,"E63.1.0.10")])]});
            var Q10;
            Q10=makeQuery(id+"F1.opExtrude","SWEPT_EDGE",EDGE,{"disambiguationData":[OSD([sQuery(id+"F0.wireOp",EDGE,"E63.1.0.1"),sQuery(id+"F0.wireOp",EDGE,"E63.1.0.4")])]});
            var Q11;
            Q11=makeQuery(id+"F1.opExtrude","SWEPT_EDGE",EDGE,{"disambiguationData":[OSD([sQuery(id+"F0.wireOp",EDGE,"E63.1.0.2"),sQuery(id+"F0.wireOp",EDGE,"E63.1.0.4")])]});
            var Q12;
            Q12=makeQuery(id+"F1.opExtrude","SWEPT_EDGE",EDGE,{"disambiguationData":[OSD([sQuery(id+"F0.wireOp",EDGE,"E63.1.0.0"),sQuery(id+"F0.wireOp",EDGE,"E63.1.0.5")])]});
            var Q13;
            Q13=makeQuery(id+"F1.opExtrude","SWEPT_EDGE",EDGE,{"disambiguationData":[OSD([sQuery(id+"F0.wireOp",EDGE,"E63.1.0.2"),sQuery(id+"F0.wireOp",EDGE,"E63.1.0.10")])]});
            var Q14;
            Q14=makeQuery(id+"F1.opExtrude","SWEPT_EDGE",EDGE,{"disambiguationData":[OSD([sQuery(id+"F0.wireOp",EDGE,"E63.1.0.0"),sQuery(id+"F0.wireOp",EDGE,"E63.1.0.9")])]});
            var Q15;
            Q15=makeQuery(id+"F1.opExtrude","SWEPT_EDGE",EDGE,{"disambiguationData":[OSD([sQuery(id+"F0.wireOp",EDGE,"E63.1.0.3"),sQuery(id+"F0.wireOp",EDGE,"E63.1.0.5")])]});
            var Q16;
            Q16=makeQuery(id+"F1.opExtrude","SWEPT_EDGE",EDGE,{"disambiguationData":[OSD([sQuery(id+"F0.wireOp",EDGE,"E63.2.0.3"),sQuery(id+"F0.wireOp",EDGE,"E63.2.0.5")])]});
            var Q17;
            Q17=makeQuery(id+"F1.opExtrude","SWEPT_EDGE",EDGE,{"disambiguationData":[OSD([sQuery(id+"F0.wireOp",EDGE,"E63.2.0.1"),sQuery(id+"F0.wireOp",EDGE,"E63.2.0.10")])]});
            var Q18;
            Q18=makeQuery(id+"F1.opExtrude","SWEPT_EDGE",EDGE,{"disambiguationData":[OSD([sQuery(id+"F0.wireOp",EDGE,"E63.2.0.2"),sQuery(id+"F0.wireOp",EDGE,"E63.2.0.10")])]});
            var Q19;
            Q19=makeQuery(id+"F1.opExtrude","SWEPT_EDGE",EDGE,{"disambiguationData":[OSD([sQuery(id+"F0.wireOp",EDGE,"E63.2.0.1"),sQuery(id+"F0.wireOp",EDGE,"E63.2.0.4")])]});
            var Q20;
            Q20=makeQuery(id+"F1.opExtrude","SWEPT_EDGE",EDGE,{"disambiguationData":[OSD([sQuery(id+"F0.wireOp",EDGE,"E63.2.0.0"),sQuery(id+"F0.wireOp",EDGE,"E63.2.0.9")])]});
            var Q21;
            Q21=makeQuery(id+"F1.opExtrude","SWEPT_EDGE",EDGE,{"disambiguationData":[OSD([sQuery(id+"F0.wireOp",EDGE,"E63.2.0.2"),sQuery(id+"F0.wireOp",EDGE,"E63.2.0.4")])]});
            var Q22;
            Q22=makeQuery(id+"F1.opExtrude","SWEPT_EDGE",EDGE,{"disambiguationData":[OSD([sQuery(id+"F0.wireOp",EDGE,"E63.2.0.0"),sQuery(id+"F0.wireOp",EDGE,"E63.2.0.5")])]});
            var Q23;
            Q23=makeQuery(id+"F1.opExtrude","SWEPT_EDGE",EDGE,{"disambiguationData":[OSD([sQuery(id+"F0.wireOp",EDGE,"E63.2.0.3"),sQuery(id+"F0.wireOp",EDGE,"E63.2.0.9")])]});
            chamfer(context, id + "F4", {"entities" : qUnion([Q0, Q1, Q2, Q3, Q4, Q5, Q6, Q7, Q8, Q9, Q10, Q11, Q12, Q13, Q14, Q15, Q16, Q17, Q18, Q19, Q20, Q21, Q22, Q23]), "width" : 1 * mm, "tangentPropagation" : true});
        }
        {
            var Q0;
            Q0=makeQuery(id+"F1.opExtrude","SWEPT_EDGE",EDGE,{"disambiguationData":[OSD([sQuery(id+"F0.wireOp",EDGE,"E64.bottom"),sQuery(id+"F0.wireOp",EDGE,"E64.right")])]});
            var Q1;
            Q1=makeQuery(id+"F1.opExtrude","SWEPT_EDGE",EDGE,{"disambiguationData":[OSD([sQuery(id+"F0.wireOp",EDGE,"E64.bottom"),sQuery(id+"F0.wireOp",EDGE,"E64.left")])]});
            var Q2;
            Q2=makeQuery(id+"F1.opExtrude","SWEPT_EDGE",EDGE,{"disambiguationData":[OSD([sQuery(id+"F0.wireOp",EDGE,"E65.bottom"),sQuery(id+"F0.wireOp",EDGE,"E65.right")])]});
            var Q3;
            Q3=makeQuery(id+"F1.opExtrude","SWEPT_EDGE",EDGE,{"disambiguationData":[OSD([sQuery(id+"F0.wireOp",EDGE,"E65.bottom"),sQuery(id+"F0.wireOp",EDGE,"E65.left")])]});
            var Q4;
            Q4=makeQuery(id+"F1.opExtrude","SWEPT_EDGE",EDGE,{"disambiguationData":[OSD([sQuery(id+"F0.wireOp",EDGE,"E66.bottom"),sQuery(id+"F0.wireOp",EDGE,"E66.left")])]});
            var Q5;
            Q5=makeQuery(id+"F1.opExtrude","SWEPT_EDGE",EDGE,{"disambiguationData":[OSD([sQuery(id+"F0.wireOp",EDGE,"E66.bottom"),sQuery(id+"F0.wireOp",EDGE,"E66.right")])]});
            var Q6;
            Q6=makeQuery(id+"F1.opExtrude","SWEPT_EDGE",EDGE,{"disambiguationData":[OSD([sQuery(id+"F0.wireOp",EDGE,"E83.1.0.12"),sQuery(id+"F0.wireOp",EDGE,"E83.1.0.23")])]});
            var Q7;
            Q7=makeQuery(id+"F1.opExtrude","SWEPT_EDGE",EDGE,{"disambiguationData":[OSD([sQuery(id+"F0.wireOp",EDGE,"E83.1.0.23"),sQuery(id+"F0.wireOp",EDGE,"E83.1.0.24")])]});
            var Q8;
            Q8=makeQuery(id+"F1.opExtrude","SWEPT_EDGE",EDGE,{"disambiguationData":[OSD([sQuery(id+"F0.wireOp",EDGE,"E83.1.0.16"),sQuery(id+"F0.wireOp",EDGE,"E83.1.0.19")])]});
            var Q9;
            Q9=makeQuery(id+"F1.opExtrude","SWEPT_EDGE",EDGE,{"disambiguationData":[OSD([sQuery(id+"F0.wireOp",EDGE,"E83.1.0.18"),sQuery(id+"F0.wireOp",EDGE,"E83.1.0.19")])]});
            var Q10;
            Q10=makeQuery(id+"F1.opExtrude","SWEPT_EDGE",EDGE,{"disambiguationData":[OSD([sQuery(id+"F0.wireOp",EDGE,"E83.1.0.4"),sQuery(id+"F0.wireOp",EDGE,"E83.1.0.13")])]});
            var Q11;
            Q11=makeQuery(id+"F1.opExtrude","SWEPT_EDGE",EDGE,{"disambiguationData":[OSD([sQuery(id+"F0.wireOp",EDGE,"E83.1.0.4"),sQuery(id+"F0.wireOp",EDGE,"E83.1.0.26")])]});
            var Q12;
            Q12=makeQuery(id+"F1.opExtrude","SWEPT_EDGE",EDGE,{"disambiguationData":[OSD([sQuery(id+"F0.wireOp",EDGE,"E69.top"),sQuery(id+"F0.wireOp",EDGE,"E69.left")])]});
            var Q13;
            Q13=makeQuery(id+"F1.opExtrude","SWEPT_EDGE",EDGE,{"disambiguationData":[OSD([sQuery(id+"F0.wireOp",EDGE,"E83.1.0.0"),sQuery(id+"F0.wireOp",EDGE,"E83.1.0.11")])]});
            var Q14;
            Q14=makeQuery(id+"F1.opExtrude","SWEPT_EDGE",EDGE,{"disambiguationData":[OSD([sQuery(id+"F0.wireOp",EDGE,"E67.top"),sQuery(id+"F0.wireOp",EDGE,"E67.right")])]});
            var Q15;
            Q15=makeQuery(id+"F1.opExtrude","SWEPT_EDGE",EDGE,{"disambiguationData":[OSD([sQuery(id+"F0.wireOp",EDGE,"E67.bottom"),sQuery(id+"F0.wireOp",EDGE,"E67.left")])]});
            var Q16;
            Q16=makeQuery(id+"F1.opExtrude","SWEPT_EDGE",EDGE,{"disambiguationData":[OSD([sQuery(id+"F0.wireOp",EDGE,"E67.top"),sQuery(id+"F0.wireOp",EDGE,"E67.left")])]});
            var Q17;
            Q17=makeQuery(id+"F1.opExtrude","SWEPT_EDGE",EDGE,{"disambiguationData":[OSD([sQuery(id+"F0.wireOp",EDGE,"E67.bottom"),sQuery(id+"F0.wireOp",EDGE,"E67.right")])]});
            var Q18;
            Q18=makeQuery(id+"F1.opExtrude","SWEPT_EDGE",EDGE,{"disambiguationData":[OSD([sQuery(id+"F0.wireOp",EDGE,"E64.top"),sQuery(id+"F0.wireOp",EDGE,"E64.right")])]});
            var Q19;
            Q19=makeQuery(id+"F1.opExtrude","SWEPT_EDGE",EDGE,{"disambiguationData":[OSD([sQuery(id+"F0.wireOp",EDGE,"E64.top"),sQuery(id+"F0.wireOp",EDGE,"E64.left")])]});
            var Q20;
            Q20=makeQuery(id+"F1.opExtrude","SWEPT_EDGE",EDGE,{"disambiguationData":[OSD([sQuery(id+"F0.wireOp",EDGE,"E68.bottom"),sQuery(id+"F0.wireOp",EDGE,"E68.right")])]});
            var Q21;
            Q21=makeQuery(id+"F1.opExtrude","SWEPT_EDGE",EDGE,{"disambiguationData":[OSD([sQuery(id+"F0.wireOp",EDGE,"E65.top"),sQuery(id+"F0.wireOp",EDGE,"E65.left")])]});
            var Q22;
            Q22=makeQuery(id+"F1.opExtrude","SWEPT_EDGE",EDGE,{"disambiguationData":[OSD([sQuery(id+"F0.wireOp",EDGE,"E65.top"),sQuery(id+"F0.wireOp",EDGE,"E65.right")])]});
            var Q23;
            Q23=makeQuery(id+"F1.opExtrude","SWEPT_EDGE",EDGE,{"disambiguationData":[OSD([sQuery(id+"F0.wireOp",EDGE,"E68.bottom"),sQuery(id+"F0.wireOp",EDGE,"E68.left")])]});
            var Q24;
            Q24=makeQuery(id+"F1.opExtrude","SWEPT_EDGE",EDGE,{"disambiguationData":[OSD([sQuery(id+"F0.wireOp",EDGE,"E68.top"),sQuery(id+"F0.wireOp",EDGE,"E68.left")])]});
            var Q25;
            Q25=makeQuery(id+"F1.opExtrude","SWEPT_EDGE",EDGE,{"disambiguationData":[OSD([sQuery(id+"F0.wireOp",EDGE,"E68.top"),sQuery(id+"F0.wireOp",EDGE,"E68.right")])]});
            var Q26;
            Q26=makeQuery(id+"F1.opExtrude","SWEPT_EDGE",EDGE,{"disambiguationData":[OSD([sQuery(id+"F0.wireOp",EDGE,"E66.top"),sQuery(id+"F0.wireOp",EDGE,"E66.right")])]});
            var Q27;
            Q27=makeQuery(id+"F1.opExtrude","SWEPT_EDGE",EDGE,{"disambiguationData":[OSD([sQuery(id+"F0.wireOp",EDGE,"E83.1.0.14"),sQuery(id+"F0.wireOp",EDGE,"E83.1.0.24")])]});
            var Q28;
            Q28=makeQuery(id+"F1.opExtrude","SWEPT_EDGE",EDGE,{"disambiguationData":[OSD([sQuery(id+"F0.wireOp",EDGE,"E69.bottom"),sQuery(id+"F0.wireOp",EDGE,"E69.left")])]});
            var Q29;
            Q29=makeQuery(id+"F1.opExtrude","SWEPT_EDGE",EDGE,{"disambiguationData":[OSD([sQuery(id+"F0.wireOp",EDGE,"E69.bottom"),sQuery(id+"F0.wireOp",EDGE,"E69.right")])]});
            var Q30;
            Q30=makeQuery(id+"F1.opExtrude","SWEPT_EDGE",EDGE,{"disambiguationData":[OSD([sQuery(id+"F0.wireOp",EDGE,"E83.1.0.9"),sQuery(id+"F0.wireOp",EDGE,"E83.1.0.25")])]});
            var Q31;
            Q31=makeQuery(id+"F1.opExtrude","SWEPT_EDGE",EDGE,{"disambiguationData":[OSD([sQuery(id+"F0.wireOp",EDGE,"E83.1.0.12"),sQuery(id+"F0.wireOp",EDGE,"E83.1.0.14")])]});
            var Q32;
            Q32=makeQuery(id+"F1.opExtrude","SWEPT_EDGE",EDGE,{"disambiguationData":[OSD([sQuery(id+"F0.wireOp",EDGE,"E66.top"),sQuery(id+"F0.wireOp",EDGE,"E66.left")])]});
            var Q33;
            Q33=makeQuery(id+"F1.opExtrude","SWEPT_EDGE",EDGE,{"disambiguationData":[OSD([sQuery(id+"F0.wireOp",EDGE,"E69.top"),sQuery(id+"F0.wireOp",EDGE,"E69.right")])]});
            var Q34;
            Q34=makeQuery(id+"F1.opExtrude","SWEPT_EDGE",EDGE,{"disambiguationData":[OSD([sQuery(id+"F0.wireOp",EDGE,"E83.1.0.9"),sQuery(id+"F0.wireOp",EDGE,"E83.1.0.11")])]});
            var Q35;
            Q35=makeQuery(id+"F1.opExtrude","SWEPT_EDGE",EDGE,{"disambiguationData":[OSD([sQuery(id+"F0.wireOp",EDGE,"E83.1.0.6"),sQuery(id+"F0.wireOp",EDGE,"E83.1.0.16")])]});
            var Q36;
            Q36=makeQuery(id+"F1.opExtrude","SWEPT_EDGE",EDGE,{"disambiguationData":[OSD([sQuery(id+"F0.wireOp",EDGE,"E83.1.0.0"),sQuery(id+"F0.wireOp",EDGE,"E83.1.0.25")])]});
            var Q37;
            Q37=makeQuery(id+"F1.opExtrude","SWEPT_EDGE",EDGE,{"disambiguationData":[OSD([sQuery(id+"F0.wireOp",EDGE,"E83.1.0.2"),sQuery(id+"F0.wireOp",EDGE,"E83.1.0.20")])]});
            var Q38;
            Q38=makeQuery(id+"F1.opExtrude","SWEPT_EDGE",EDGE,{"disambiguationData":[OSD([sQuery(id+"F0.wireOp",EDGE,"E83.1.0.6"),sQuery(id+"F0.wireOp",EDGE,"E83.1.0.18")])]});
            var Q39;
            Q39=makeQuery(id+"F1.opExtrude","SWEPT_EDGE",EDGE,{"disambiguationData":[OSD([sQuery(id+"F0.wireOp",EDGE,"E83.1.0.2"),sQuery(id+"F0.wireOp",EDGE,"E83.1.0.5")])]});
            var Q40;
            Q40=makeQuery(id+"F1.opExtrude","SWEPT_EDGE",EDGE,{"disambiguationData":[OSD([sQuery(id+"F0.wireOp",EDGE,"E83.1.0.3"),sQuery(id+"F0.wireOp",EDGE,"E83.1.0.21")])]});
            var Q41;
            Q41=makeQuery(id+"F1.opExtrude","SWEPT_EDGE",EDGE,{"disambiguationData":[OSD([sQuery(id+"F0.wireOp",EDGE,"E83.1.0.7"),sQuery(id+"F0.wireOp",EDGE,"E83.1.0.13")])]});
            var Q42;
            Q42=makeQuery(id+"F1.opExtrude","SWEPT_EDGE",EDGE,{"disambiguationData":[OSD([sQuery(id+"F0.wireOp",EDGE,"E83.1.0.7"),sQuery(id+"F0.wireOp",EDGE,"E83.1.0.26")])]});
            var Q43;
            Q43=makeQuery(id+"F1.opExtrude","SWEPT_EDGE",EDGE,{"disambiguationData":[OSD([sQuery(id+"F0.wireOp",EDGE,"E83.1.0.8"),sQuery(id+"F0.wireOp",EDGE,"E83.1.0.20")])]});
            var Q44;
            Q44=makeQuery(id+"F1.opExtrude","SWEPT_EDGE",EDGE,{"disambiguationData":[OSD([sQuery(id+"F0.wireOp",EDGE,"E83.1.0.5"),sQuery(id+"F0.wireOp",EDGE,"E83.1.0.8")])]});
            var Q45;
            Q45=makeQuery(id+"F1.opExtrude","SWEPT_EDGE",EDGE,{"disambiguationData":[OSD([sQuery(id+"F0.wireOp",EDGE,"E83.1.0.21"),sQuery(id+"F0.wireOp",EDGE,"E83.1.0.22")])]});
            var Q46;
            Q46=makeQuery(id+"F1.opExtrude","SWEPT_EDGE",EDGE,{"disambiguationData":[OSD([sQuery(id+"F0.wireOp",EDGE,"E83.1.0.1"),sQuery(id+"F0.wireOp",EDGE,"E83.1.0.3")])]});
            var Q47;
            Q47=makeQuery(id+"F1.opExtrude","SWEPT_EDGE",EDGE,{"disambiguationData":[OSD([sQuery(id+"F0.wireOp",EDGE,"E83.1.0.1"),sQuery(id+"F0.wireOp",EDGE,"E83.1.0.22")])]});
            var Q48;
            Q48=makeQuery(id+"F1.opExtrude","SWEPT_EDGE",EDGE,{"disambiguationData":[OSD([sQuery(id+"F0.wireOp",EDGE,"E83.2.0.12"),sQuery(id+"F0.wireOp",EDGE,"E83.2.0.23")])]});
            var Q49;
            Q49=makeQuery(id+"F1.opExtrude","SWEPT_EDGE",EDGE,{"disambiguationData":[OSD([sQuery(id+"F0.wireOp",EDGE,"E83.2.0.23"),sQuery(id+"F0.wireOp",EDGE,"E83.2.0.24")])]});
            var Q50;
            Q50=makeQuery(id+"F1.opExtrude","SWEPT_EDGE",EDGE,{"disambiguationData":[OSD([sQuery(id+"F0.wireOp",EDGE,"E83.2.0.9"),sQuery(id+"F0.wireOp",EDGE,"E83.2.0.11")])]});
            var Q51;
            Q51=makeQuery(id+"F1.opExtrude","SWEPT_EDGE",EDGE,{"disambiguationData":[OSD([sQuery(id+"F0.wireOp",EDGE,"E83.2.0.12"),sQuery(id+"F0.wireOp",EDGE,"E83.2.0.14")])]});
            var Q52;
            Q52=makeQuery(id+"F1.opExtrude","SWEPT_EDGE",EDGE,{"disambiguationData":[OSD([sQuery(id+"F0.wireOp",EDGE,"E83.2.0.0"),sQuery(id+"F0.wireOp",EDGE,"E83.2.0.11")])]});
            var Q53;
            Q53=makeQuery(id+"F1.opExtrude","SWEPT_EDGE",EDGE,{"disambiguationData":[OSD([sQuery(id+"F0.wireOp",EDGE,"E83.2.0.0"),sQuery(id+"F0.wireOp",EDGE,"E83.2.0.25")])]});
            var Q54;
            Q54=makeQuery(id+"F1.opExtrude","SWEPT_EDGE",EDGE,{"disambiguationData":[OSD([sQuery(id+"F0.wireOp",EDGE,"E83.2.0.14"),sQuery(id+"F0.wireOp",EDGE,"E83.2.0.24")])]});
            var Q55;
            Q55=makeQuery(id+"F1.opExtrude","SWEPT_EDGE",EDGE,{"disambiguationData":[OSD([sQuery(id+"F0.wireOp",EDGE,"E83.2.0.9"),sQuery(id+"F0.wireOp",EDGE,"E83.2.0.25")])]});
            var Q56;
            Q56=makeQuery(id+"F1.opExtrude","SWEPT_EDGE",EDGE,{"disambiguationData":[OSD([sQuery(id+"F0.wireOp",EDGE,"E83.2.0.2"),sQuery(id+"F0.wireOp",EDGE,"E83.2.0.5")])]});
            var Q57;
            Q57=makeQuery(id+"F1.opExtrude","SWEPT_EDGE",EDGE,{"disambiguationData":[OSD([sQuery(id+"F0.wireOp",EDGE,"E83.2.0.16"),sQuery(id+"F0.wireOp",EDGE,"E83.2.0.19")])]});
            var Q58;
            Q58=makeQuery(id+"F1.opExtrude","SWEPT_EDGE",EDGE,{"disambiguationData":[OSD([sQuery(id+"F0.wireOp",EDGE,"E83.2.0.6"),sQuery(id+"F0.wireOp",EDGE,"E83.2.0.16")])]});
            var Q59;
            Q59=makeQuery(id+"F1.opExtrude","SWEPT_EDGE",EDGE,{"disambiguationData":[OSD([sQuery(id+"F0.wireOp",EDGE,"E83.2.0.6"),sQuery(id+"F0.wireOp",EDGE,"E83.2.0.18")])]});
            var Q60;
            Q60=makeQuery(id+"F1.opExtrude","SWEPT_EDGE",EDGE,{"disambiguationData":[OSD([sQuery(id+"F0.wireOp",EDGE,"E83.2.0.7"),sQuery(id+"F0.wireOp",EDGE,"E83.2.0.13")])]});
            var Q61;
            Q61=makeQuery(id+"F1.opExtrude","SWEPT_EDGE",EDGE,{"disambiguationData":[OSD([sQuery(id+"F0.wireOp",EDGE,"E83.2.0.4"),sQuery(id+"F0.wireOp",EDGE,"E83.2.0.13")])]});
            var Q62;
            Q62=makeQuery(id+"F1.opExtrude","SWEPT_EDGE",EDGE,{"disambiguationData":[OSD([sQuery(id+"F0.wireOp",EDGE,"E83.2.0.7"),sQuery(id+"F0.wireOp",EDGE,"E83.2.0.26")])]});
            var Q63;
            Q63=makeQuery(id+"F1.opExtrude","SWEPT_EDGE",EDGE,{"disambiguationData":[OSD([sQuery(id+"F0.wireOp",EDGE,"E83.2.0.2"),sQuery(id+"F0.wireOp",EDGE,"E83.2.0.20")])]});
            var Q64;
            Q64=makeQuery(id+"F1.opExtrude","SWEPT_EDGE",EDGE,{"disambiguationData":[OSD([sQuery(id+"F0.wireOp",EDGE,"E83.2.0.18"),sQuery(id+"F0.wireOp",EDGE,"E83.2.0.19")])]});
            var Q65;
            Q65=makeQuery(id+"F1.opExtrude","SWEPT_EDGE",EDGE,{"disambiguationData":[OSD([sQuery(id+"F0.wireOp",EDGE,"E83.2.0.8"),sQuery(id+"F0.wireOp",EDGE,"E83.2.0.20")])]});
            var Q66;
            Q66=makeQuery(id+"F1.opExtrude","SWEPT_EDGE",EDGE,{"disambiguationData":[OSD([sQuery(id+"F0.wireOp",EDGE,"E83.2.0.5"),sQuery(id+"F0.wireOp",EDGE,"E83.2.0.8")])]});
            var Q67;
            Q67=makeQuery(id+"F1.opExtrude","SWEPT_EDGE",EDGE,{"disambiguationData":[OSD([sQuery(id+"F0.wireOp",EDGE,"E83.2.0.3"),sQuery(id+"F0.wireOp",EDGE,"E83.2.0.21")])]});
            var Q68;
            Q68=makeQuery(id+"F1.opExtrude","SWEPT_EDGE",EDGE,{"disambiguationData":[OSD([sQuery(id+"F0.wireOp",EDGE,"E83.2.0.1"),sQuery(id+"F0.wireOp",EDGE,"E83.2.0.22")])]});
            var Q69;
            Q69=makeQuery(id+"F1.opExtrude","SWEPT_EDGE",EDGE,{"disambiguationData":[OSD([sQuery(id+"F0.wireOp",EDGE,"E83.2.0.4"),sQuery(id+"F0.wireOp",EDGE,"E83.2.0.26")])]});
            var Q70;
            Q70=makeQuery(id+"F1.opExtrude","SWEPT_EDGE",EDGE,{"disambiguationData":[OSD([sQuery(id+"F0.wireOp",EDGE,"E83.2.0.21"),sQuery(id+"F0.wireOp",EDGE,"E83.2.0.22")])]});
            var Q71;
            Q71=makeQuery(id+"F1.opExtrude","SWEPT_EDGE",EDGE,{"disambiguationData":[OSD([sQuery(id+"F0.wireOp",EDGE,"E83.2.0.1"),sQuery(id+"F0.wireOp",EDGE,"E83.2.0.3")])]});
            chamfer(context, id + "F5", {"entities" : qUnion([Q0, Q1, Q2, Q3, Q4, Q5, Q6, Q7, Q8, Q9, Q10, Q11, Q12, Q13, Q14, Q15, Q16, Q17, Q18, Q19, Q20, Q21, Q22, Q23, Q24, Q25, Q26, Q27, Q28, Q29, Q30, Q31, Q32, Q33, Q34, Q35, Q36, Q37, Q38, Q39, Q40, Q41, Q42, Q43, Q44, Q45, Q46, Q47, Q48, Q49, Q50, Q51, Q52, Q53, Q54, Q55, Q56, Q57, Q58, Q59, Q60, Q61, Q62, Q63, Q64, Q65, Q66, Q67, Q68, Q69, Q70, Q71]), "width" : 0.5 * mm, "tangentPropagation" : true});
        }
        {
            var Q0;
            Q0=makeQuery(id+"F0.imprint","IMPRINT",FACE,{"disambiguationData":[TD([[makeQuery(id+"F0.imprint","IMPRINT",EDGE,{"derivedFrom":sQuery(id+"F0.wireOp",EDGE,"E31.bottom")}),1.0]])]});
            var Q1;
            {var subQ0=sQuery(id+"F0.wireOp",EDGE,"E107");Q1=makeQuery(id+"F0.imprint","IMPRINT",FACE,{"disambiguationData":[TD([[makeQuery(id+"F0.imprint","IMPRINT",EDGE,{"derivedFrom":subQ0}),-1.0]])]});}
            var Q2;
            {var subQ0=sQuery(id+"F0.wireOp",EDGE,"E109.MirrorCS");Q2=makeQuery(id+"F0.imprint","IMPRINT",FACE,{"disambiguationData":[TD([[makeQuery(id+"F0.imprint","IMPRINT",EDGE,{"derivedFrom":subQ0}),1.0]])]});}
            var Q3;
            {var subQ0=sQuery(id+"F0.wireOp",EDGE,"E105.MirrorCS");Q3=makeQuery(id+"F0.imprint","IMPRINT",FACE,{"disambiguationData":[TD([[makeQuery(id+"F0.imprint","IMPRINT",EDGE,{"derivedFrom":subQ0}),1.0]])]});}
            var Q4;
            {var subQ0=sQuery(id+"F0.wireOp",EDGE,"E96");Q4=makeQuery(id+"F0.imprint","IMPRINT",FACE,{"disambiguationData":[TD([[makeQuery(id+"F0.imprint","IMPRINT",EDGE,{"derivedFrom":subQ0}),-1.0]])]});}
            var Q5;
            {var subQ0=sQuery(id+"F0.wireOp",EDGE,"E103.MirrorCS");Q5=makeQuery(id+"F0.imprint","IMPRINT",FACE,{"disambiguationData":[TD([[makeQuery(id+"F0.imprint","IMPRINT",EDGE,{"derivedFrom":subQ0}),1.0]])]});}
            var Q6;
            {var subQ0=sQuery(id+"F0.wireOp",EDGE,"E95");Q6=makeQuery(id+"F0.imprint","IMPRINT",FACE,{"disambiguationData":[TD([[makeQuery(id+"F0.imprint","IMPRINT",EDGE,{"derivedFrom":subQ0}),-1.0]])]});}
            var Q7;
            {var subQ0=sQuery(id+"F0.wireOp",EDGE,"E101.MirrorCS");Q7=makeQuery(id+"F0.imprint","IMPRINT",FACE,{"disambiguationData":[TD([[makeQuery(id+"F0.imprint","IMPRINT",EDGE,{"derivedFrom":subQ0}),1.0]])]});}
            var Q8;
            {var subQ0=sQuery(id+"F0.wireOp",EDGE,"E94");Q8=makeQuery(id+"F0.imprint","IMPRINT",FACE,{"disambiguationData":[TD([[makeQuery(id+"F0.imprint","IMPRINT",EDGE,{"derivedFrom":subQ0}),-1.0]])]});}
            var Q9;
            Q9=makeQuery(id+"F0.imprint","IMPRINT",FACE,{"disambiguationData":[TD([[makeQuery(id+"F0.imprint","IMPRINT",EDGE,{"derivedFrom":sQuery(id+"F0.wireOp",EDGE,"E53.sketch_text.stroke-0")}),1.0]])]});
            var Q10;
            Q10=makeQuery(id+"F0.imprint","IMPRINT",FACE,{"disambiguationData":[TD([[makeQuery(id+"F0.imprint","IMPRINT",EDGE,{"derivedFrom":sQuery(id+"F0.wireOp",EDGE,"E54.sketch_text.stroke-0")}),1.0]])]});
            var Q11;
            Q11=makeQuery(id+"F0.imprint","IMPRINT",FACE,{"disambiguationData":[TD([[makeQuery(id+"F0.imprint","IMPRINT",EDGE,{"derivedFrom":sQuery(id+"F0.wireOp",EDGE,"E88.sketch_text.stroke-0")}),1.0]])]});
            var Q12;
            Q12=makeQuery(id+"F0.imprint","IMPRINT",FACE,{"disambiguationData":[TD([[makeQuery(id+"F0.imprint","IMPRINT",EDGE,{"derivedFrom":sQuery(id+"F0.wireOp",EDGE,"E55.sketch_text.stroke-0")}),1.0]])]});
            var Q13;
            Q13=makeQuery(id+"F0.imprint","IMPRINT",FACE,{"disambiguationData":[TD([[makeQuery(id+"F0.imprint","IMPRINT",EDGE,{"derivedFrom":sQuery(id+"F0.wireOp",EDGE,"E111.sketch_text.stroke-0")}),1.0]])]});
            var Q14;
            {var subQ0=sQuery(id+"F0.wireOp",EDGE,"E118.MirrorCS");Q14=makeQuery(id+"F0.imprint","IMPRINT",FACE,{"disambiguationData":[TD([[makeQuery(id+"F0.imprint","IMPRINT",EDGE,{"derivedFrom":subQ0}),1.0]])]});}
            var Q15;
            {var subQ0=sQuery(id+"F0.wireOp",EDGE,"E116");Q15=makeQuery(id+"F0.imprint","IMPRINT",FACE,{"disambiguationData":[TD([[makeQuery(id+"F0.imprint","IMPRINT",EDGE,{"derivedFrom":subQ0}),-1.0]])]});}
            extrude(context, id + "F6", {"entities" : qUnion([Q0, Q1, Q2, Q3, Q4, Q5, Q6, Q7, Q8, Q9, Q10, Q11, Q12, Q13, Q14, Q15]), "depth" : 3 * mm, "offsetDistance" : 25 * mm});
        }
        {
            var Q0;
            Q0=makeQuery(id+"F6.opExtrude","SWEPT_EDGE",EDGE,{"disambiguationData":[OSD([sQuery(id+"F0.wireOp",EDGE,"E31.bottom"),sQuery(id+"F0.wireOp",EDGE,"E31.right")])]});
            var Q1;
            Q1=makeQuery(id+"F6.opExtrude","SWEPT_EDGE",EDGE,{"disambiguationData":[OSD([sQuery(id+"F0.wireOp",EDGE,"E31.top"),sQuery(id+"F0.wireOp",EDGE,"E31.right")])]});
            var Q2;
            Q2=makeQuery(id+"F6.opExtrude","SWEPT_EDGE",EDGE,{"disambiguationData":[OSD([sQuery(id+"F0.wireOp",EDGE,"E31.top"),sQuery(id+"F0.wireOp",EDGE,"E31.left")])]});
            var Q3;
            Q3=makeQuery(id+"F6.opExtrude","SWEPT_EDGE",EDGE,{"disambiguationData":[OSD([sQuery(id+"F0.wireOp",EDGE,"E31.bottom"),sQuery(id+"F0.wireOp",EDGE,"E31.left")])]});
            chamfer(context, id + "F7", {"entities" : qUnion([Q0, Q1, Q2, Q3]), "width" : 3 * mm, "tangentPropagation" : true});
        }
        {
            var Q0;
            Q0=makeQuery(id+"F6.opExtrude","SWEPT_EDGE",EDGE,{"disambiguationData":[OSD([sQuery(id+"F0.wireOp",EDGE,"E42"),sQuery(id+"F0.wireOp",EDGE,"E43")])]});
            var Q1;
            Q1=makeQuery(id+"F6.opExtrude","SWEPT_EDGE",EDGE,{"disambiguationData":[OSD([sQuery(id+"F0.wireOp",EDGE,"E43"),sQuery(id+"F0.wireOp",EDGE,"E44")])]});
            var Q2;
            Q2=makeQuery(id+"F6.opExtrude","SWEPT_EDGE",EDGE,{"disambiguationData":[OSD([sQuery(id+"F0.wireOp",EDGE,"E46"),sQuery(id+"F0.wireOp",EDGE,"E47")])]});
            var Q3;
            Q3=makeQuery(id+"F6.opExtrude","SWEPT_EDGE",EDGE,{"disambiguationData":[OSD([sQuery(id+"F0.wireOp",EDGE,"E45"),sQuery(id+"F0.wireOp",EDGE,"E46")])]});
            chamfer(context, id + "F8", {"entities" : qUnion([Q0, Q1, Q2, Q3]), "width" : 2 * mm, "tangentPropagation" : true});
        }
        {
            var Q0;
            Q0=makeQuery(id+"F6.opExtrude","SWEPT_EDGE",EDGE,{"disambiguationData":[OSD([sQuery(id+"F0.wireOp",EDGE,"E86.bottom"),sQuery(id+"F0.wireOp",EDGE,"E86.right")])]});
            var Q1;
            Q1=makeQuery(id+"F6.opExtrude","SWEPT_EDGE",EDGE,{"disambiguationData":[OSD([sQuery(id+"F0.wireOp",EDGE,"E84.top"),sQuery(id+"F0.wireOp",EDGE,"E84.right")])]});
            var Q2;
            Q2=makeQuery(id+"F6.opExtrude","SWEPT_EDGE",EDGE,{"disambiguationData":[OSD([sQuery(id+"F0.wireOp",EDGE,"E84.top"),sQuery(id+"F0.wireOp",EDGE,"E84.left")])]});
            var Q3;
            Q3=makeQuery(id+"F6.opExtrude","SWEPT_EDGE",EDGE,{"disambiguationData":[OSD([sQuery(id+"F0.wireOp",EDGE,"E84.bottom"),sQuery(id+"F0.wireOp",EDGE,"E84.left")])]});
            var Q4;
            Q4=makeQuery(id+"F6.opExtrude","SWEPT_EDGE",EDGE,{"disambiguationData":[OSD([sQuery(id+"F0.wireOp",EDGE,"E86.bottom"),sQuery(id+"F0.wireOp",EDGE,"E86.left")])]});
            var Q5;
            Q5=makeQuery(id+"F6.opExtrude","SWEPT_EDGE",EDGE,{"disambiguationData":[OSD([sQuery(id+"F0.wireOp",EDGE,"E84.bottom"),sQuery(id+"F0.wireOp",EDGE,"E84.right")])]});
            var Q6;
            Q6=makeQuery(id+"F6.opExtrude","SWEPT_EDGE",EDGE,{"disambiguationData":[OSD([sQuery(id+"F0.wireOp",EDGE,"E86.top"),sQuery(id+"F0.wireOp",EDGE,"E86.left")])]});
            var Q7;
            Q7=makeQuery(id+"F6.opExtrude","SWEPT_EDGE",EDGE,{"disambiguationData":[OSD([sQuery(id+"F0.wireOp",EDGE,"E86.top"),sQuery(id+"F0.wireOp",EDGE,"E86.right")])]});
            var Q8;
            Q8=makeQuery(id+"F6.opExtrude","SWEPT_EDGE",EDGE,{"disambiguationData":[OSD([sQuery(id+"F0.wireOp",EDGE,"E113.top"),sQuery(id+"F0.wireOp",EDGE,"E113.left")])]});
            var Q9;
            Q9=makeQuery(id+"F6.opExtrude","SWEPT_EDGE",EDGE,{"disambiguationData":[OSD([sQuery(id+"F0.wireOp",EDGE,"E113.top"),sQuery(id+"F0.wireOp",EDGE,"E113.right")])]});
            var Q10;
            Q10=makeQuery(id+"F6.opExtrude","SWEPT_EDGE",EDGE,{"disambiguationData":[OSD([sQuery(id+"F0.wireOp",EDGE,"E113.bottom"),sQuery(id+"F0.wireOp",EDGE,"E113.right")])]});
            var Q11;
            Q11=makeQuery(id+"F6.opExtrude","SWEPT_EDGE",EDGE,{"disambiguationData":[OSD([sQuery(id+"F0.wireOp",EDGE,"E113.bottom"),sQuery(id+"F0.wireOp",EDGE,"E113.left")])]});
            var Q12;
            Q12=makeQuery(id+"F6.opExtrude","SWEPT_EDGE",EDGE,{"disambiguationData":[OSD([sQuery(id+"F0.wireOp",EDGE,"E114.bottom"),sQuery(id+"F0.wireOp",EDGE,"E114.right")])]});
            var Q13;
            Q13=makeQuery(id+"F6.opExtrude","SWEPT_EDGE",EDGE,{"disambiguationData":[OSD([sQuery(id+"F0.wireOp",EDGE,"E114.top"),sQuery(id+"F0.wireOp",EDGE,"E114.right")])]});
            var Q14;
            Q14=makeQuery(id+"F6.opExtrude","SWEPT_EDGE",EDGE,{"disambiguationData":[OSD([sQuery(id+"F0.wireOp",EDGE,"E114.bottom"),sQuery(id+"F0.wireOp",EDGE,"E114.left")])]});
            var Q15;
            Q15=makeQuery(id+"F6.opExtrude","SWEPT_EDGE",EDGE,{"disambiguationData":[OSD([sQuery(id+"F0.wireOp",EDGE,"E114.top"),sQuery(id+"F0.wireOp",EDGE,"E114.left")])]});
            chamfer(context, id + "F9", {"entities" : qUnion([Q0, Q1, Q2, Q3, Q4, Q5, Q6, Q7, Q8, Q9, Q10, Q11, Q12, Q13, Q14, Q15]), "width" : 1 * mm, "tangentPropagation" : true});
        }
        {
            var Q0;
            Q0=makeQuery(id+"F6.opExtrude","SWEPT_EDGE",EDGE,{"disambiguationData":[OSD([sQuery(id+"F0.wireOp",EDGE,"E85.bottom"),sQuery(id+"F0.wireOp",EDGE,"E85.right")])]});
            var Q1;
            Q1=makeQuery(id+"F6.opExtrude","SWEPT_EDGE",EDGE,{"disambiguationData":[OSD([sQuery(id+"F0.wireOp",EDGE,"E85.bottom"),sQuery(id+"F0.wireOp",EDGE,"E85.left")])]});
            var Q2;
            Q2=makeQuery(id+"F6.opExtrude","SWEPT_EDGE",EDGE,{"disambiguationData":[OSD([sQuery(id+"F0.wireOp",EDGE,"E87.bottom"),sQuery(id+"F0.wireOp",EDGE,"E87.left")])]});
            var Q3;
            Q3=makeQuery(id+"F6.opExtrude","SWEPT_EDGE",EDGE,{"disambiguationData":[OSD([sQuery(id+"F0.wireOp",EDGE,"E87.bottom"),sQuery(id+"F0.wireOp",EDGE,"E87.right")])]});
            var Q4;
            Q4=makeQuery(id+"F6.opExtrude","SWEPT_EDGE",EDGE,{"disambiguationData":[OSD([sQuery(id+"F0.wireOp",EDGE,"E91.top"),sQuery(id+"F0.wireOp",EDGE,"E91.right")])]});
            var Q5;
            Q5=makeQuery(id+"F6.opExtrude","SWEPT_EDGE",EDGE,{"disambiguationData":[OSD([sQuery(id+"F0.wireOp",EDGE,"E90.top"),sQuery(id+"F0.wireOp",EDGE,"E90.left")])]});
            var Q6;
            Q6=makeQuery(id+"F6.opExtrude","SWEPT_EDGE",EDGE,{"disambiguationData":[OSD([sQuery(id+"F0.wireOp",EDGE,"E91.top"),sQuery(id+"F0.wireOp",EDGE,"E91.left")])]});
            var Q7;
            Q7=makeQuery(id+"F6.opExtrude","SWEPT_EDGE",EDGE,{"disambiguationData":[OSD([sQuery(id+"F0.wireOp",EDGE,"E90.top"),sQuery(id+"F0.wireOp",EDGE,"E90.right")])]});
            var Q8;
            Q8=makeQuery(id+"F6.opExtrude","SWEPT_EDGE",EDGE,{"disambiguationData":[OSD([sQuery(id+"F0.wireOp",EDGE,"E91.bottom"),sQuery(id+"F0.wireOp",EDGE,"E91.left")])]});
            var Q9;
            Q9=makeQuery(id+"F6.opExtrude","SWEPT_EDGE",EDGE,{"disambiguationData":[OSD([sQuery(id+"F0.wireOp",EDGE,"E90.bottom"),sQuery(id+"F0.wireOp",EDGE,"E90.right")])]});
            var Q10;
            Q10=makeQuery(id+"F6.opExtrude","SWEPT_EDGE",EDGE,{"disambiguationData":[OSD([sQuery(id+"F0.wireOp",EDGE,"E90.bottom"),sQuery(id+"F0.wireOp",EDGE,"E90.left")])]});
            var Q11;
            Q11=makeQuery(id+"F6.opExtrude","SWEPT_EDGE",EDGE,{"disambiguationData":[OSD([sQuery(id+"F0.wireOp",EDGE,"E91.bottom"),sQuery(id+"F0.wireOp",EDGE,"E91.right")])]});
            var Q12;
            Q12=makeQuery(id+"F6.opExtrude","SWEPT_EDGE",EDGE,{"disambiguationData":[OSD([sQuery(id+"F0.wireOp",EDGE,"E85.top"),sQuery(id+"F0.wireOp",EDGE,"E85.left")])]});
            var Q13;
            Q13=makeQuery(id+"F6.opExtrude","SWEPT_EDGE",EDGE,{"disambiguationData":[OSD([sQuery(id+"F0.wireOp",EDGE,"E85.top"),sQuery(id+"F0.wireOp",EDGE,"E85.right")])]});
            var Q14;
            Q14=makeQuery(id+"F6.opExtrude","SWEPT_EDGE",EDGE,{"disambiguationData":[OSD([sQuery(id+"F0.wireOp",EDGE,"E87.top"),sQuery(id+"F0.wireOp",EDGE,"E87.left")])]});
            var Q15;
            Q15=makeQuery(id+"F6.opExtrude","SWEPT_EDGE",EDGE,{"disambiguationData":[OSD([sQuery(id+"F0.wireOp",EDGE,"E87.top"),sQuery(id+"F0.wireOp",EDGE,"E87.right")])]});
            var Q16;
            Q16=makeQuery(id+"F6.opExtrude","SWEPT_EDGE",EDGE,{"disambiguationData":[OSD([sQuery(id+"F0.wireOp",EDGE,"E89.top"),sQuery(id+"F0.wireOp",EDGE,"E89.right")])]});
            var Q17;
            Q17=makeQuery(id+"F6.opExtrude","SWEPT_EDGE",EDGE,{"disambiguationData":[OSD([sQuery(id+"F0.wireOp",EDGE,"E89.top"),sQuery(id+"F0.wireOp",EDGE,"E89.left")])]});
            var Q18;
            Q18=makeQuery(id+"F6.opExtrude","SWEPT_EDGE",EDGE,{"disambiguationData":[OSD([sQuery(id+"F0.wireOp",EDGE,"E89.bottom"),sQuery(id+"F0.wireOp",EDGE,"E89.left")])]});
            var Q19;
            Q19=makeQuery(id+"F6.opExtrude","SWEPT_EDGE",EDGE,{"disambiguationData":[OSD([sQuery(id+"F0.wireOp",EDGE,"E92.bottom"),sQuery(id+"F0.wireOp",EDGE,"E92.right")])]});
            var Q20;
            Q20=makeQuery(id+"F6.opExtrude","SWEPT_EDGE",EDGE,{"disambiguationData":[OSD([sQuery(id+"F0.wireOp",EDGE,"E92.bottom"),sQuery(id+"F0.wireOp",EDGE,"E92.left")])]});
            var Q21;
            Q21=makeQuery(id+"F6.opExtrude","SWEPT_EDGE",EDGE,{"disambiguationData":[OSD([sQuery(id+"F0.wireOp",EDGE,"E89.bottom"),sQuery(id+"F0.wireOp",EDGE,"E89.right")])]});
            var Q22;
            Q22=makeQuery(id+"F6.opExtrude","SWEPT_EDGE",EDGE,{"disambiguationData":[OSD([sQuery(id+"F0.wireOp",EDGE,"E92.top"),sQuery(id+"F0.wireOp",EDGE,"E92.left")])]});
            var Q23;
            Q23=makeQuery(id+"F6.opExtrude","SWEPT_EDGE",EDGE,{"disambiguationData":[OSD([sQuery(id+"F0.wireOp",EDGE,"E92.top"),sQuery(id+"F0.wireOp",EDGE,"E92.right")])]});
            chamfer(context, id + "F10", {"entities" : qUnion([Q0, Q1, Q2, Q3, Q4, Q5, Q6, Q7, Q8, Q9, Q10, Q11, Q12, Q13, Q14, Q15, Q16, Q17, Q18, Q19, Q20, Q21, Q22, Q23]), "width" : 0.5 * mm, "tangentPropagation" : true});
        }
    });
